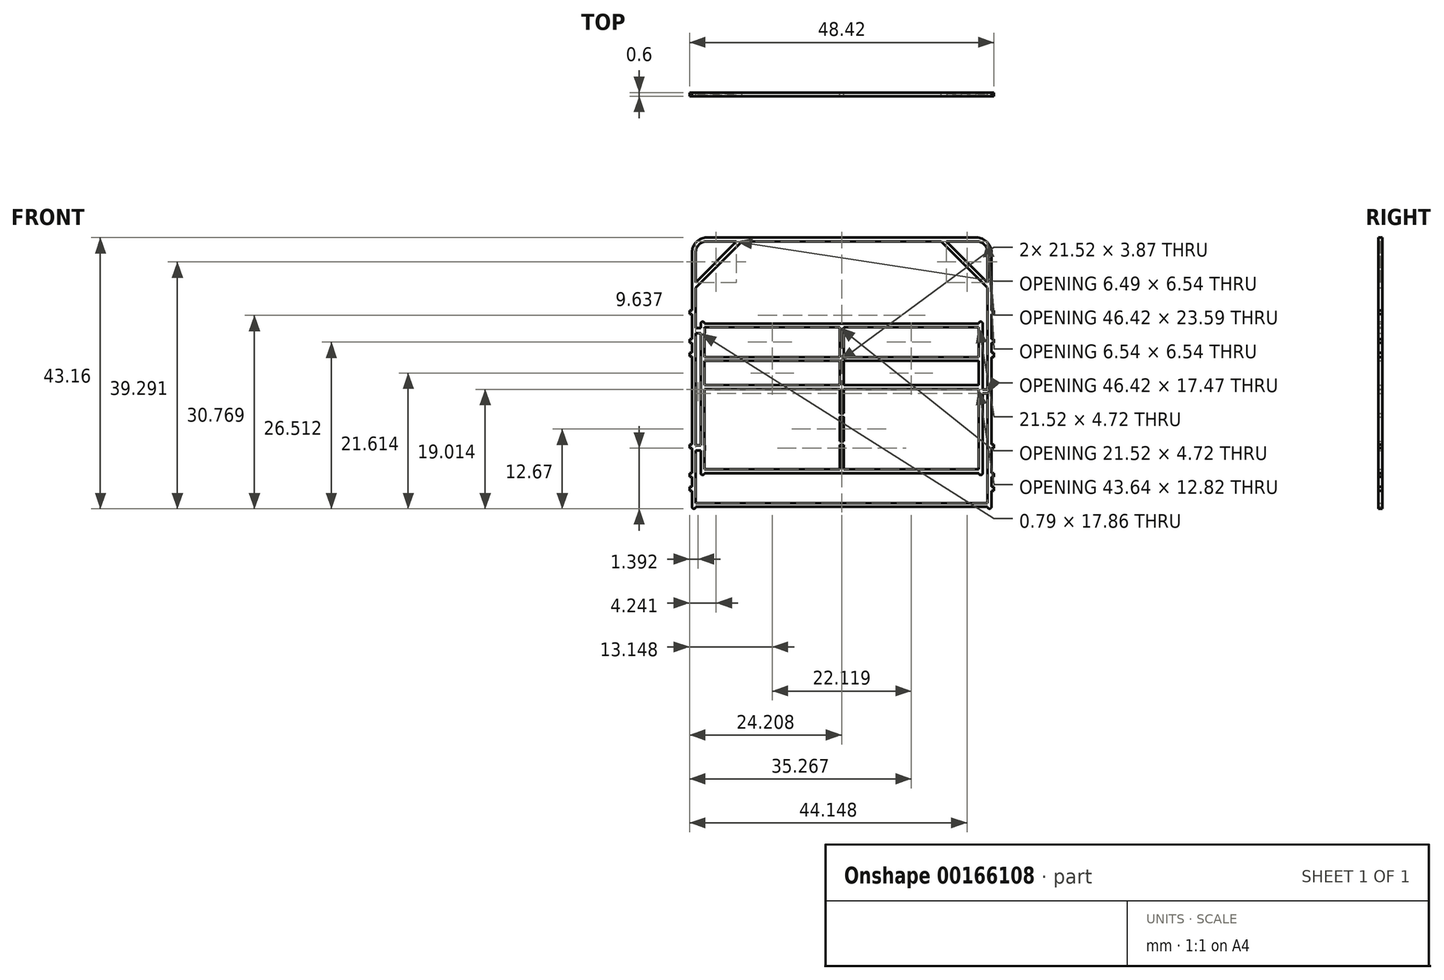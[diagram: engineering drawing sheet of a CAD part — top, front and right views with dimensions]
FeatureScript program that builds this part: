
annotation { "Feature Type Name" : "Feature", "Feature Type Description" : "" }
export const myFeature = defineFeature(function(context is Context, id is Id, definition is map)
    precondition{}
    {
        {
            var Q0;
            Q0=qCreatedBy(makeId("Front.planeOp"),FACE);
            var sketch = newSketch(context, id + "F0", { "sketchPlane" : qUnion([Q0])});
            skLineSegment(sketch, "E0.top", {"start": v(-2.38, 42.86) * mm, "end": v(-45.24, 42.86) * mm});
            skLineSegment(sketch, "E0.left", {"start": v(0, 0) * mm, "end": v(0, 40.48) * mm});
            skLineSegment(sketch, "E0.right", {"start": v(-47.63, 0) * mm, "end": v(-47.63, 40.48) * mm});
            skLineSegment(sketch, "E1.0", {"start": v(-0.6, 0.6) * mm, "end": v(-47.03, 0.6) * mm});
            skLineSegment(sketch, "E2.0", {"start": v(-47.03, 0) * mm, "end": v(-47.03, 9) * mm});
            skLineSegment(sketch, "E3.0", {"start": v(-0.6, 0) * mm, "end": v(-0.6, 40.48) * mm});
            skLineSegment(sketch, "E4.0", {"start": v(-2.38, 42.26) * mm, "end": v(-45.24, 42.26) * mm});
            skPoint(sketch, "E5.visualSharp", {"position": v(-47.63, 42.86) * mm});
            skArc(sketch, "E5.filletArc", {"start": v(-45.24, 42.86) * mm, "mid": v(-46.93, 42.17) * mm, "end": v(-47.63, 40.48) * mm});
            skArc(sketch, "E6", {"start": v(-45.24, 42.26) * mm, "mid": v(-46.5, 41.74) * mm, "end": v(-47.03, 40.48) * mm});
            skLineSegment(sketch, "E7", {"start": v(-47.03, 35.72) * mm, "end": v(-40.53, 42.26) * mm});
            skLineSegment(sketch, "E8.0", {"start": v(-46.6, 35.3) * mm, "end": v(-40.1, 41.84) * mm});
            skLineSegment(sketch, "E9", {"start": v(-46.6, 35.3) * mm, "end": v(-47.02, 34.87) * mm});
            skLineSegment(sketch, "E10", {"start": v(-40.1, 41.84) * mm, "end": v(-39.69, 42.26) * mm});
            skPoint(sketch, "E11.visualSharp", {"position": v(0, 42.86) * mm});
            skArc(sketch, "E11.filletArc", {"start": v(0, 40.48) * mm, "mid": v(-0.7, 42.17) * mm, "end": v(-2.38, 42.86) * mm});
            skPoint(sketch, "E12", {"position": v(-2.38, 42.26) * mm});
            skPoint(sketch, "E13", {"position": v(-0.6, 40.48) * mm});
            skArc(sketch, "E14", {"start": v(-0.6, 40.48) * mm, "mid": v(-1.12, 41.74) * mm, "end": v(-2.38, 42.26) * mm});
            skLineSegment(sketch, "E15", {"start": v(-7.14, 42.26) * mm, "end": v(-0.6, 35.72) * mm});
            skLineSegment(sketch, "E16.0", {"start": v(-7.57, 41.84) * mm, "end": v(-1.02, 35.3) * mm});
            skLineSegment(sketch, "E17", {"start": v(-7.57, 41.84) * mm, "end": v(-8, 42.26) * mm});
            skLineSegment(sketch, "E18", {"start": v(-1.02, 35.3) * mm, "end": v(-0.6, 34.87) * mm});
            skLineSegment(sketch, "E19", {"start": v(-45.63, 5.36) * mm, "end": v(-2, 5.36) * mm});
            skLineSegment(sketch, "E20.trimOffspring", {"start": v(-46.23, 35.67) * mm, "end": v(-46.23, 35.72) * mm, "construction": true});
            skLineSegment(sketch, "E21", {"start": v(-46.23, 5.36) * mm, "end": v(-46.23, 9) * mm});
            skLineSegment(sketch, "E22.0", {"start": v(-45.63, 5.36) * mm, "end": v(-45.63, 9) * mm});
            skLineSegment(sketch, "E23.trimOffspring", {"start": v(-1.4, 35.66) * mm, "end": v(-1.4, 35.72) * mm, "construction": true});
            skLineSegment(sketch, "E24", {"start": v(-1.4, 5.36) * mm, "end": v(-1.4, 29.18) * mm});
            skLineSegment(sketch, "E25.0", {"start": v(-2, 5.36) * mm, "end": v(-2, 29.18) * mm});
            skLineSegment(sketch, "E26", {"start": v(-45.63, 29.18) * mm, "end": v(-2, 29.18) * mm});
            skLineSegment(sketch, "E27.0", {"start": v(-45.63, 28.57) * mm, "end": v(-2, 28.58) * mm});
            skLineSegment(sketch, "E28.trimOffspring", {"start": v(-2, 5.36) * mm, "end": v(-45.63, 5.36) * mm, "construction": true});
            skLineSegment(sketch, "E29.trimOffspring", {"start": v(-2, 5.96) * mm, "end": v(-45.63, 5.96) * mm});
            skArc(sketch, "E30", {"start": v(-46.23, 5.36) * mm, "mid": v(-45.93, 5.06) * mm, "end": v(-45.63, 5.36) * mm});
            skArc(sketch, "E31", {"start": v(-2, 5.36) * mm, "mid": v(-1.7, 5.06) * mm, "end": v(-1.4, 5.36) * mm});
            skArc(sketch, "E32", {"start": v(-1.4, 29.18) * mm, "mid": v(-1.7, 29.48) * mm, "end": v(-2, 29.18) * mm});
            skArc(sketch, "E33", {"start": v(-45.63, 29.18) * mm, "mid": v(-45.93, 29.47) * mm, "end": v(-46.23, 29.18) * mm});
            skArc(sketch, "E34", {"start": v(-47.63, 0) * mm, "mid": v(-47.33, -0.3) * mm, "end": v(-47.03, 0) * mm});
            skArc(sketch, "E35", {"start": v(-0.6, 0) * mm, "mid": v(-0.3, -0.3) * mm, "end": v(0, 0) * mm});
            skLineSegment(sketch, "E36.trimOffspring", {"start": v(-0.6, 0) * mm, "end": v(-47.03, 0) * mm});
            skLineSegment(sketch, "E37.trimOffspring", {"start": v(-46.23, 35.72) * mm, "end": v(-46.18, 35.72) * mm, "construction": true});
            skPoint(sketch, "E38.start.orphan", {"position": v(-48.55, 42.86) * mm});
            skPoint(sketch, "E39.start.orphan", {"position": v(0, 43.64) * mm});
            skPoint(sketch, "E40.start.orphan", {"position": v(0.52, 42.86) * mm});
            skLineSegment(sketch, "E41.trimOffspring", {"start": v(-1.4, 35.72) * mm, "end": v(-1.45, 35.72) * mm, "construction": true});
            skLineSegment(sketch, "E42.0", {"start": v(-2, 9.83) * mm, "end": v(-45.63, 9.83) * mm});
            skLineSegment(sketch, "E43.0", {"start": v(-2, 10.43) * mm, "end": v(-45.63, 10.43) * mm});
            skLineSegment(sketch, "E44.0", {"start": v(-2, 14.3) * mm, "end": v(-45.63, 14.3) * mm});
            skLineSegment(sketch, "E45.0", {"start": v(-2, 14.9) * mm, "end": v(-45.63, 14.9) * mm});
            skLineSegment(sketch, "E46.0", {"start": v(-2, 18.78) * mm, "end": v(-45.63, 18.78) * mm});
            skLineSegment(sketch, "E47.0", {"start": v(-2, 19.38) * mm, "end": v(-45.63, 19.38) * mm});
            skLineSegment(sketch, "E48.0", {"start": v(-2, 23.25) * mm, "end": v(-45.63, 23.25) * mm});
            skLineSegment(sketch, "E49.0", {"start": v(-2, 23.85) * mm, "end": v(-45.63, 23.85) * mm});
            skPoint(sketch, "E50.endSnap0", {"position": v(-23.81, 28.58) * mm});
            skLineSegment(sketch, "E51.0", {"start": v(-24.11, 28.58) * mm, "end": v(-24.11, 23.85) * mm});
            skLineSegment(sketch, "E52.0", {"start": v(-23.51, 28.58) * mm, "end": v(-23.51, 23.85) * mm});
            skPoint(sketch, "E50.start.orphan", {"position": v(-23.81, 30.6) * mm});
            skPoint(sketch, "E53.orphan", {"position": v(-2, 30.6) * mm});
            skPoint(sketch, "E54.orphan", {"position": v(-45.63, 30.6) * mm});
            skPoint(sketch, "E55.orphan", {"position": v(-23.81, 2.6) * mm});
            skLineSegment(sketch, "E56.trimOffspring", {"start": v(-24.11, 14.3) * mm, "end": v(-24.11, 10.43) * mm});
            skLineSegment(sketch, "E57.trimOffspring", {"start": v(-23.51, 14.3) * mm, "end": v(-23.51, 10.43) * mm});
            skLineSegment(sketch, "E58.trimOffspring", {"start": v(-24.11, 9.83) * mm, "end": v(-24.11, 5.96) * mm});
            skLineSegment(sketch, "E59.trimOffspring", {"start": v(-23.51, 9.83) * mm, "end": v(-23.51, 5.96) * mm});
            skLineSegment(sketch, "E60.trimOffspring", {"start": v(-23.51, 18.78) * mm, "end": v(-23.51, 14.9) * mm});
            skLineSegment(sketch, "E61.trimOffspring", {"start": v(-24.11, 18.78) * mm, "end": v(-24.11, 14.9) * mm});
            skLineSegment(sketch, "E62.trimOffspring", {"start": v(-24.11, 23.25) * mm, "end": v(-24.11, 19.38) * mm});
            skLineSegment(sketch, "E63.trimOffspring", {"start": v(-23.51, 23.25) * mm, "end": v(-23.51, 19.38) * mm});
            skLineSegment(sketch, "E64.bottom", {"start": v(-45.58, 9.79) * mm, "end": v(-47.62, 9.79) * mm});
            skLineSegment(sketch, "E64.top", {"start": v(-45.58, 9) * mm, "end": v(-47.63, 9) * mm});
            skLineSegment(sketch, "E64.left", {"start": v(-45.58, 9.79) * mm, "end": v(-45.58, 9) * mm});
            skLineSegment(sketch, "E64.right", {"start": v(-47.63, 9.79) * mm, "end": v(-47.63, 9) * mm});
            skLineSegment(sketch, "E65.trimOffspring", {"start": v(-47.03, 9.79) * mm, "end": v(-47.03, 27.64) * mm});
            skLineSegment(sketch, "E66.trimOffspring", {"start": v(-46.23, 9.79) * mm, "end": v(-46.23, 27.64) * mm});
            skLineSegment(sketch, "E67.trimOffspring", {"start": v(-45.63, 9.79) * mm, "end": v(-45.63, 27.64) * mm});
            skLineSegment(sketch, "E68.bottom", {"start": v(-45.57, 28.44) * mm, "end": v(-47.63, 28.44) * mm});
            skLineSegment(sketch, "E68.top", {"start": v(-45.57, 27.64) * mm, "end": v(-47.63, 27.64) * mm});
            skLineSegment(sketch, "E68.left", {"start": v(-45.57, 28.44) * mm, "end": v(-45.57, 27.64) * mm});
            skLineSegment(sketch, "E68.right", {"start": v(-47.63, 28.44) * mm, "end": v(-47.63, 27.64) * mm});
            skLineSegment(sketch, "E69.trimOffspring", {"start": v(-46.23, 28.44) * mm, "end": v(-46.23, 29.18) * mm});
            skLineSegment(sketch, "E70.trimOffspring", {"start": v(-45.63, 28.44) * mm, "end": v(-45.63, 29.18) * mm});
            skLineSegment(sketch, "E71.trimOffspring", {"start": v(-47.03, 28.44) * mm, "end": v(-47.03, 40.48) * mm});
            skLineSegment(sketch, "E72.bottom", {"start": v(-47.63, 5.36) * mm, "end": v(-48.02, 5.36) * mm});
            skLineSegment(sketch, "E72.top", {"start": v(-47.62, 4.77) * mm, "end": v(-48.02, 4.77) * mm});
            skLineSegment(sketch, "E72.left", {"start": v(-47.63, 5.36) * mm, "end": v(-47.63, 4.77) * mm});
            skLineSegment(sketch, "E72.right", {"start": v(-48.02, 5.36) * mm, "end": v(-48.02, 4.77) * mm});
            skLineSegment(sketch, "E73.bottom", {"start": v(-48.02, 3.18) * mm, "end": v(-47.63, 3.18) * mm});
            skLineSegment(sketch, "E73.top", {"start": v(-48.02, 2.58) * mm, "end": v(-47.63, 2.58) * mm});
            skLineSegment(sketch, "E73.left", {"start": v(-48.02, 3.18) * mm, "end": v(-48.02, 2.58) * mm});
            skLineSegment(sketch, "E73.right", {"start": v(-47.63, 3.18) * mm, "end": v(-47.63, 2.58) * mm});
            skLineSegment(sketch, "E74.bottom", {"start": v(-48.02, 9.93) * mm, "end": v(-47.62, 9.93) * mm});
            skLineSegment(sketch, "E74.top", {"start": v(-48.02, 9.33) * mm, "end": v(-47.62, 9.33) * mm});
            skLineSegment(sketch, "E74.left", {"start": v(-48.02, 9.93) * mm, "end": v(-48.02, 9.33) * mm});
            skLineSegment(sketch, "E74.right", {"start": v(-47.63, 9.93) * mm, "end": v(-47.63, 9.33) * mm});
            skLineSegment(sketch, "E75.bottom", {"start": v(0, 3.18) * mm, "end": v(0.4, 3.18) * mm});
            skLineSegment(sketch, "E75.top", {"start": v(0, 2.58) * mm, "end": v(0.4, 2.58) * mm});
            skLineSegment(sketch, "E75.left", {"start": v(0, 3.18) * mm, "end": v(0, 2.58) * mm});
            skLineSegment(sketch, "E75.right", {"start": v(0.4, 3.18) * mm, "end": v(0.4, 2.58) * mm});
            skLineSegment(sketch, "E76.bottom", {"start": v(0, 5.36) * mm, "end": v(0.4, 5.36) * mm});
            skLineSegment(sketch, "E76.top", {"start": v(0, 4.77) * mm, "end": v(0.4, 4.77) * mm});
            skLineSegment(sketch, "E76.left", {"start": v(0, 5.36) * mm, "end": v(0, 4.77) * mm});
            skLineSegment(sketch, "E76.right", {"start": v(0.4, 5.36) * mm, "end": v(0.4, 4.77) * mm});
            skLineSegment(sketch, "E77.bottom", {"start": v(0, 9.93) * mm, "end": v(0.4, 9.93) * mm});
            skLineSegment(sketch, "E77.top", {"start": v(0, 9.33) * mm, "end": v(0.4, 9.33) * mm});
            skLineSegment(sketch, "E77.left", {"start": v(0, 9.93) * mm, "end": v(0, 9.33) * mm});
            skLineSegment(sketch, "E77.right", {"start": v(0.4, 9.93) * mm, "end": v(0.4, 9.33) * mm});
            skLineSegment(sketch, "E78.bottom", {"start": v(-47.63, 24.52) * mm, "end": v(-48.02, 24.52) * mm});
            skLineSegment(sketch, "E78.top", {"start": v(-47.63, 23.93) * mm, "end": v(-48.02, 23.93) * mm});
            skLineSegment(sketch, "E78.left", {"start": v(-47.63, 24.52) * mm, "end": v(-47.63, 23.93) * mm});
            skLineSegment(sketch, "E78.right", {"start": v(-48.02, 24.52) * mm, "end": v(-48.02, 23.93) * mm});
            skLineSegment(sketch, "E79.bottom", {"start": v(-47.63, 26.7) * mm, "end": v(-48.02, 26.7) * mm});
            skLineSegment(sketch, "E79.top", {"start": v(-47.63, 26.1) * mm, "end": v(-48.02, 26.1) * mm});
            skLineSegment(sketch, "E79.left", {"start": v(-47.63, 26.7) * mm, "end": v(-47.63, 26.1) * mm});
            skLineSegment(sketch, "E79.right", {"start": v(-48.02, 26.7) * mm, "end": v(-48.02, 26.1) * mm});
            skLineSegment(sketch, "E80.bottom", {"start": v(-47.63, 31.27) * mm, "end": v(-48.02, 31.27) * mm});
            skLineSegment(sketch, "E80.top", {"start": v(-47.63, 30.67) * mm, "end": v(-48.02, 30.67) * mm});
            skLineSegment(sketch, "E80.left", {"start": v(-47.63, 31.27) * mm, "end": v(-47.63, 30.67) * mm});
            skLineSegment(sketch, "E80.right", {"start": v(-48.02, 31.27) * mm, "end": v(-48.02, 30.67) * mm});
            skLineSegment(sketch, "E81.bottom", {"start": v(0, 24.52) * mm, "end": v(0.4, 24.52) * mm});
            skLineSegment(sketch, "E81.top", {"start": v(0, 23.85) * mm, "end": v(0.4, 23.85) * mm});
            skLineSegment(sketch, "E81.left", {"start": v(0, 24.52) * mm, "end": v(0, 23.85) * mm});
            skLineSegment(sketch, "E81.right", {"start": v(0.4, 24.52) * mm, "end": v(0.4, 23.85) * mm});
            skLineSegment(sketch, "E82.bottom", {"start": v(0, 26.7) * mm, "end": v(0.4, 26.7) * mm});
            skLineSegment(sketch, "E82.top", {"start": v(0, 26.1) * mm, "end": v(0.4, 26.1) * mm});
            skLineSegment(sketch, "E82.left", {"start": v(0, 26.7) * mm, "end": v(0, 26.1) * mm});
            skLineSegment(sketch, "E82.right", {"start": v(0.4, 26.7) * mm, "end": v(0.4, 26.1) * mm});
            skLineSegment(sketch, "E83.bottom", {"start": v(0, 31.27) * mm, "end": v(0.4, 31.27) * mm});
            skLineSegment(sketch, "E83.top", {"start": v(0, 30.67) * mm, "end": v(0.4, 30.67) * mm});
            skLineSegment(sketch, "E83.left", {"start": v(0, 31.27) * mm, "end": v(0, 30.67) * mm});
            skLineSegment(sketch, "E83.right", {"start": v(0.4, 31.27) * mm, "end": v(0.4, 30.67) * mm});
            skLineSegment(sketch, "E84.bottom", {"start": v(-2, 14.3) * mm, "end": v(-3.58, 14.3) * mm});
            skLineSegment(sketch, "E84.top", {"start": v(-2, 10.43) * mm, "end": v(-3.58, 10.43) * mm});
            skLineSegment(sketch, "E84.left", {"start": v(-2, 14.3) * mm, "end": v(-2, 10.43) * mm});
            skLineSegment(sketch, "E84.right", {"start": v(-3.58, 14.3) * mm, "end": v(-3.58, 10.43) * mm});
            skLineSegment(sketch, "E85.bottom", {"start": v(-9.52, 18.78) * mm, "end": v(-2, 18.78) * mm});
            skLineSegment(sketch, "E85.right", {"start": v(-2, 18.78) * mm, "end": v(-2, 17.98) * mm});
            skLineSegment(sketch, "E86", {"start": v(-2, 17.98) * mm, "end": v(-5.96, 17.98) * mm});
            skLineSegment(sketch, "E87", {"start": v(-5.96, 17.98) * mm, "end": v(-5.96, 18.78) * mm});
            skLineSegment(sketch, "E88", {"start": v(-3.58, 14.9) * mm, "end": v(-3.58, 17.98) * mm});
            skLineSegment(sketch, "E89.bottom", {"start": v(-1.4, 18.67) * mm, "end": v(-0.6, 18.67) * mm});
            skLineSegment(sketch, "E89.top", {"start": v(-1.4, 18.07) * mm, "end": v(-0.6, 18.07) * mm});
            skLineSegment(sketch, "E89.left", {"start": v(-1.4, 18.67) * mm, "end": v(-1.4, 18.07) * mm});
            skLineSegment(sketch, "E89.right", {"start": v(-0.6, 18.67) * mm, "end": v(-0.6, 18.07) * mm});
            skSolve(sketch);
        }
        {
            var Q0;
            {var subQ1=sQuery(id+"F0.wireOp",EDGE,"E7");Q0=makeQuery(id+"F0.imprint","IMPRINT",FACE,{"disambiguationData":[TD([[makeQuery(id+"F0.imprint","IMPRINT",EDGE,{"derivedFrom":subQ1}),-1.0]])]});}
            var Q1;
            Q1=makeQuery(id+"F0.imprint","IMPRINT",FACE,{"disambiguationData":[TD([[makeQuery(id+"F0.imprint","IMPRINT",EDGE,{"derivedFrom":sQuery(id+"F0.wireOp",EDGE,"E0.top")}),1.0]])]});
            var Q2;
            {var subQ0=sQuery(id+"F0.wireOp",EDGE,"E15");Q2=makeQuery(id+"F0.imprint","IMPRINT",FACE,{"disambiguationData":[TD([[makeQuery(id+"F0.imprint","IMPRINT",EDGE,{"derivedFrom":subQ0}),-1.0]])]});}
            var Q3;
            {var subQ4=sQuery(id+"F0.wireOp",EDGE,"E26");Q3=makeQuery(id+"F0.imprint","IMPRINT",FACE,{"disambiguationData":[TD([[makeQuery(id+"F0.imprint","IMPRINT",EDGE,{"derivedFrom":subQ4}),-1.0]])]});}
            var Q4;
            {var subQ1=sQuery(id+"F0.wireOp",EDGE,"E48.0");var subQ5=sQuery(id+"F0.wireOp",EDGE,"E25.0");var subQ6=makeQuery(id+"F0.imprint","INTERSECT",VERTEX,{"derivedFrom":[subQ5,subQ1]});Q4=makeQuery(id+"F0.imprint","IMPRINT",FACE,{"disambiguationData":[TD([[makeQuery(id+"F0.imprint","IMPRINT",EDGE,{"disambiguationData":[TD([[subQ6,-1.0]])],"derivedFrom":subQ5}),1.0]])]});}
            var Q5;
            {var subQ1=sQuery(id+"F0.wireOp",EDGE,"E46.0");var subQ4=sQuery(id+"F0.wireOp",EDGE,"E85.bottom");var subQ5=makeQuery(id+"F0.imprint","INTERSECT",VERTEX,{"derivedFrom":[subQ1,subQ4]});Q5=makeQuery(id+"F0.imprint","IMPRINT",FACE,{"disambiguationData":[TD([[makeQuery(id+"F0.imprint","IMPRINT",EDGE,{"disambiguationData":[TD([[subQ5,-1.0]])],"derivedFrom":subQ1}),-1.0]])]});}
            var Q6;
            {var subQ5=sQuery(id+"F0.wireOp",EDGE,"E84.bottom");Q6=makeQuery(id+"F0.imprint","IMPRINT",FACE,{"disambiguationData":[TD([[makeQuery(id+"F0.imprint","IMPRINT",EDGE,{"derivedFrom":subQ5}),-1.0]])]});}
            var Q7;
            {var subQ7=sQuery(id+"F0.wireOp",EDGE,"E84.top");Q7=makeQuery(id+"F0.imprint","IMPRINT",FACE,{"disambiguationData":[TD([[makeQuery(id+"F0.imprint","IMPRINT",EDGE,{"derivedFrom":subQ7}),1.0]])]});}
            var Q8;
            {var subQ5=sQuery(id+"F0.wireOp",EDGE,"E19");Q8=makeQuery(id+"F0.imprint","IMPRINT",FACE,{"disambiguationData":[TD([[makeQuery(id+"F0.imprint","IMPRINT",EDGE,{"derivedFrom":subQ5}),1.0]])]});}
            var Q9;
            {var subQ0=sQuery(id+"F0.wireOp",EDGE,"E58.trimOffspring");Q9=makeQuery(id+"F0.imprint","IMPRINT",FACE,{"disambiguationData":[TD([[makeQuery(id+"F0.imprint","IMPRINT",EDGE,{"derivedFrom":subQ0}),1.0]])]});}
            var Q10;
            {var subQ0=sQuery(id+"F0.wireOp",EDGE,"E56.trimOffspring");Q10=makeQuery(id+"F0.imprint","IMPRINT",FACE,{"disambiguationData":[TD([[makeQuery(id+"F0.imprint","IMPRINT",EDGE,{"derivedFrom":subQ0}),1.0]])]});}
            var Q11;
            {var subQ0=sQuery(id+"F0.wireOp",EDGE,"E60.trimOffspring");Q11=makeQuery(id+"F0.imprint","IMPRINT",FACE,{"disambiguationData":[TD([[makeQuery(id+"F0.imprint","IMPRINT",EDGE,{"derivedFrom":subQ0}),-1.0]])]});}
            var Q12;
            {var subQ0=sQuery(id+"F0.wireOp",EDGE,"E62.trimOffspring");Q12=makeQuery(id+"F0.imprint","IMPRINT",FACE,{"disambiguationData":[TD([[makeQuery(id+"F0.imprint","IMPRINT",EDGE,{"derivedFrom":subQ0}),1.0]])]});}
            var Q13;
            {var subQ0=sQuery(id+"F0.wireOp",EDGE,"E51.0");Q13=makeQuery(id+"F0.imprint","IMPRINT",FACE,{"disambiguationData":[TD([[makeQuery(id+"F0.imprint","IMPRINT",EDGE,{"derivedFrom":subQ0}),1.0]])]});}
            var Q14;
            {var subQ9=sQuery(id+"F0.wireOp",EDGE,"E66.trimOffspring");Q14=makeQuery(id+"F0.imprint","IMPRINT",FACE,{"disambiguationData":[TD([[makeQuery(id+"F0.imprint","IMPRINT",EDGE,{"derivedFrom":subQ9}),-1.0]])]});}
            var Q15;
            {var subQ5=sQuery(id+"F0.wireOp",EDGE,"E33");Q15=makeQuery(id+"F0.imprint","IMPRINT",FACE,{"disambiguationData":[TD([[makeQuery(id+"F0.imprint","IMPRINT",EDGE,{"derivedFrom":subQ5}),1.0]])]});}
            var Q16;
            {var subQ5=sQuery(id+"F0.wireOp",EDGE,"E21");Q16=makeQuery(id+"F0.imprint","IMPRINT",FACE,{"disambiguationData":[TD([[makeQuery(id+"F0.imprint","IMPRINT",EDGE,{"derivedFrom":subQ5}),-1.0]])]});}
            var Q17;
            {var subQ5=sQuery(id+"F0.wireOp",EDGE,"E31");Q17=makeQuery(id+"F0.imprint","IMPRINT",FACE,{"disambiguationData":[TD([[makeQuery(id+"F0.imprint","IMPRINT",EDGE,{"derivedFrom":subQ5}),1.0]])]});}
            var Q18;
            {var subQ3=sQuery(id+"F0.wireOp",EDGE,"E65.trimOffspring");Q18=makeQuery(id+"F0.imprint","IMPRINT",FACE,{"disambiguationData":[TD([[makeQuery(id+"F0.imprint","IMPRINT",EDGE,{"derivedFrom":subQ3}),1.0]])]});}
            var Q19;
            {var subQ2=sQuery(id+"F0.wireOp",EDGE,"E34");Q19=makeQuery(id+"F0.imprint","IMPRINT",FACE,{"disambiguationData":[TD([[makeQuery(id+"F0.imprint","IMPRINT",EDGE,{"derivedFrom":subQ2}),1.0]])]});}
            var Q20;
            Q20=makeQuery(id+"F0.imprint","IMPRINT",FACE,{"disambiguationData":[TD([[makeQuery(id+"F0.imprint","IMPRINT",EDGE,{"derivedFrom":sQuery(id+"F0.wireOp",EDGE,"E89.bottom")}),-1.0]])]});
            var Q21;
            {var subQ0=sQuery(id+"F0.wireOp",EDGE,"E1.0");Q21=makeQuery(id+"F0.imprint","IMPRINT",FACE,{"disambiguationData":[TD([[makeQuery(id+"F0.imprint","IMPRINT",EDGE,{"derivedFrom":subQ0}),1.0]])]});}
            var Q22;
            Q22=makeQuery(id+"F0.imprint","IMPRINT",FACE,{"disambiguationData":[TD([[makeQuery(id+"F0.imprint","IMPRINT",EDGE,{"derivedFrom":sQuery(id+"F0.wireOp",EDGE,"E80.bottom")}),1.0]])]});
            var Q23;
            Q23=makeQuery(id+"F0.imprint","IMPRINT",FACE,{"disambiguationData":[TD([[makeQuery(id+"F0.imprint","IMPRINT",EDGE,{"derivedFrom":sQuery(id+"F0.wireOp",EDGE,"E79.bottom")}),1.0]])]});
            var Q24;
            Q24=makeQuery(id+"F0.imprint","IMPRINT",FACE,{"disambiguationData":[TD([[makeQuery(id+"F0.imprint","IMPRINT",EDGE,{"derivedFrom":sQuery(id+"F0.wireOp",EDGE,"E78.bottom")}),1.0]])]});
            var Q25;
            {var subQ2=sQuery(id+"F0.wireOp",EDGE,"E74.bottom");Q25=makeQuery(id+"F0.imprint","IMPRINT",FACE,{"disambiguationData":[TD([[makeQuery(id+"F0.imprint","IMPRINT",EDGE,{"derivedFrom":subQ2}),-1.0]])]});}
            var Q26;
            Q26=makeQuery(id+"F0.imprint","IMPRINT",FACE,{"disambiguationData":[TD([[makeQuery(id+"F0.imprint","IMPRINT",EDGE,{"derivedFrom":sQuery(id+"F0.wireOp",EDGE,"E72.bottom")}),1.0]])]});
            var Q27;
            Q27=makeQuery(id+"F0.imprint","IMPRINT",FACE,{"disambiguationData":[TD([[makeQuery(id+"F0.imprint","IMPRINT",EDGE,{"derivedFrom":sQuery(id+"F0.wireOp",EDGE,"E73.bottom")}),-1.0]])]});
            var Q28;
            Q28=makeQuery(id+"F0.imprint","IMPRINT",FACE,{"disambiguationData":[TD([[makeQuery(id+"F0.imprint","IMPRINT",EDGE,{"derivedFrom":sQuery(id+"F0.wireOp",EDGE,"E75.bottom")}),-1.0]])]});
            var Q29;
            Q29=makeQuery(id+"F0.imprint","IMPRINT",FACE,{"disambiguationData":[TD([[makeQuery(id+"F0.imprint","IMPRINT",EDGE,{"derivedFrom":sQuery(id+"F0.wireOp",EDGE,"E76.bottom")}),-1.0]])]});
            var Q30;
            Q30=makeQuery(id+"F0.imprint","IMPRINT",FACE,{"disambiguationData":[TD([[makeQuery(id+"F0.imprint","IMPRINT",EDGE,{"derivedFrom":sQuery(id+"F0.wireOp",EDGE,"E77.bottom")}),-1.0]])]});
            var Q31;
            Q31=makeQuery(id+"F0.imprint","IMPRINT",FACE,{"disambiguationData":[TD([[makeQuery(id+"F0.imprint","IMPRINT",EDGE,{"derivedFrom":sQuery(id+"F0.wireOp",EDGE,"E83.bottom")}),-1.0]])]});
            var Q32;
            Q32=makeQuery(id+"F0.imprint","IMPRINT",FACE,{"disambiguationData":[TD([[makeQuery(id+"F0.imprint","IMPRINT",EDGE,{"derivedFrom":sQuery(id+"F0.wireOp",EDGE,"E82.bottom")}),-1.0]])]});
            var Q33;
            Q33=makeQuery(id+"F0.imprint","IMPRINT",FACE,{"disambiguationData":[TD([[makeQuery(id+"F0.imprint","IMPRINT",EDGE,{"derivedFrom":sQuery(id+"F0.wireOp",EDGE,"E81.bottom")}),-1.0]])]});
            var Q34;
            {var subQ6=sQuery(id+"F0.wireOp",EDGE,"E68.left");Q34=makeQuery(id+"F0.imprint","IMPRINT",FACE,{"disambiguationData":[TD([[makeQuery(id+"F0.imprint","IMPRINT",EDGE,{"derivedFrom":subQ6}),-1.0]])]});}
            var Q35;
            {var subQ3=sQuery(id+"F0.wireOp",EDGE,"E64.left");Q35=makeQuery(id+"F0.imprint","IMPRINT",FACE,{"disambiguationData":[TD([[makeQuery(id+"F0.imprint","IMPRINT",EDGE,{"derivedFrom":subQ3}),-1.0]])]});}
            extrude(context, id + "F1", {"entities" : qUnion([Q0, Q1, Q2, Q3, Q4, Q5, Q6, Q7, Q8, Q9, Q10, Q11, Q12, Q13, Q14, Q15, Q16, Q17, Q18, Q19, Q20, Q21, Q22, Q23, Q24, Q25, Q26, Q27, Q28, Q29, Q30, Q31, Q32, Q33, Q34, Q35]), "depth" : .6 * mm, "symmetric" : true});
        }
        {
            var Q0;
            Q0=makeQuery(id+"F1.opExtrude","CAP_EDGE",EDGE,{"disambiguationData":[OSD([sQuery(id+"F0.wireOp",EDGE,"E0.top")])],"isStart":false});
            var Q1;
            {var subQ0=sQuery(id+"F0.wireOp",EDGE,"E4.0");Q1=makeQuery(id+"F1.opExtrude","CAP_EDGE",EDGE,{"disambiguationData":[OSD([subQ0]),TDD([makeQuery(id+"F0.imprint","IMPRINT",EDGE,{"disambiguationData":[TD([[makeQuery(id+"F0.imprint","INTERSECT",VERTEX,{"derivedFrom":[subQ0,sQuery(id+"F0.wireOp",EDGE,"E10")]}),1.0]])],"derivedFrom":subQ0})])],"isStart":false});}
            var Q2;
            Q2=makeQuery(id+"F1.opExtrude","SWEPT_FACE",FACE,{"disambiguationData":[OSD([sQuery(id+"F0.wireOp",EDGE,"E0.top")])]});
            var Q3;
            Q3=makeQuery(id+"F1.opExtrude","CAP_EDGE",EDGE,{"disambiguationData":[OSD([sQuery(id+"F0.wireOp",EDGE,"E11.filletArc")])],"isStart":false});
            var Q4;
            Q4=makeQuery(id+"F1.opExtrude","CAP_EDGE",EDGE,{"disambiguationData":[OSD([sQuery(id+"F0.wireOp",EDGE,"E11.filletArc")])],"isStart":true});
            var Q5;
            Q5=makeQuery(id+"F1.opExtrude","CAP_EDGE",EDGE,{"disambiguationData":[OSD([sQuery(id+"F0.wireOp",EDGE,"E14")])],"isStart":false});
            var Q6;
            {var subQ0=sQuery(id+"F0.wireOp",EDGE,"E4.0");Q6=makeQuery(id+"F1.opExtrude","CAP_EDGE",EDGE,{"disambiguationData":[OSD([subQ0]),TDD([makeQuery(id+"F0.imprint","IMPRINT",EDGE,{"disambiguationData":[TD([[makeQuery(id+"F0.imprint","INTERSECT",VERTEX,{"derivedFrom":[subQ0,sQuery(id+"F0.wireOp",EDGE,"E14")]}),-1.0]])],"derivedFrom":subQ0})])],"isStart":false});}
            var Q7;
            Q7=makeQuery(id+"F1.opExtrude","CAP_EDGE",EDGE,{"disambiguationData":[OSD([sQuery(id+"F0.wireOp",EDGE,"E15")])],"isStart":false});
            var Q8;
            Q8=makeQuery(id+"F1.opExtrude","CAP_EDGE",EDGE,{"disambiguationData":[OSD([sQuery(id+"F0.wireOp",EDGE,"E15")])],"isStart":true});
            var Q9;
            Q9=makeQuery(id+"F1.opExtrude","CAP_EDGE",EDGE,{"disambiguationData":[OSD([sQuery(id+"F0.wireOp",EDGE,"E16.0"),sQuery(id+"F0.wireOp",EDGE,"E17"),sQuery(id+"F0.wireOp",EDGE,"E18")])],"isStart":false});
            var Q10;
            {var subQ0=sQuery(id+"F0.wireOp",EDGE,"E3.0");Q10=makeQuery(id+"F1.opExtrude","CAP_EDGE",EDGE,{"disambiguationData":[OSD([subQ0]),TDD([makeQuery(id+"F0.imprint","IMPRINT",EDGE,{"disambiguationData":[TD([[makeQuery(id+"F0.imprint","INTERSECT",VERTEX,{"derivedFrom":[subQ0,sQuery(id+"F0.wireOp",EDGE,"E14")]}),1.0]])],"derivedFrom":subQ0})])],"isStart":false});}
            var Q11;
            {var subQ0=sQuery(id+"F0.wireOp",EDGE,"E0.left");Q11=makeQuery(id+"F1.opExtrude","CAP_EDGE",EDGE,{"disambiguationData":[OSD([subQ0]),TDD([makeQuery(id+"F0.imprint","IMPRINT",EDGE,{"disambiguationData":[TD([[makeQuery(id+"F0.imprint","INTERSECT",VERTEX,{"derivedFrom":[subQ0,sQuery(id+"F0.wireOp",EDGE,"E11.filletArc")]}),1.0]])],"derivedFrom":subQ0})])],"isStart":false});}
            var Q12;
            {var subQ0=sQuery(id+"F0.wireOp",EDGE,"E0.left");Q12=makeQuery(id+"F1.opExtrude","CAP_EDGE",EDGE,{"disambiguationData":[OSD([subQ0]),TDD([makeQuery(id+"F0.imprint","IMPRINT",EDGE,{"disambiguationData":[TD([[makeQuery(id+"F0.imprint","INTERSECT",VERTEX,{"derivedFrom":[subQ0,sQuery(id+"F0.wireOp",EDGE,"E11.filletArc")]}),1.0]])],"derivedFrom":subQ0})])],"isStart":true});}
            var Q13;
            {var subQ0=sQuery(id+"F0.wireOp",EDGE,"E3.0");Q13=makeQuery(id+"F1.opExtrude","CAP_EDGE",EDGE,{"disambiguationData":[OSD([subQ0]),TDD([makeQuery(id+"F0.imprint","IMPRINT",EDGE,{"disambiguationData":[TD([[makeQuery(id+"F0.imprint","INTERSECT",VERTEX,{"derivedFrom":[subQ0,sQuery(id+"F0.wireOp",EDGE,"E18")]}),1.0]])],"derivedFrom":subQ0})])],"isStart":false});}
            var Q14;
            Q14=makeQuery(id+"F1.opExtrude","CAP_EDGE",EDGE,{"disambiguationData":[OSD([sQuery(id+"F0.wireOp",EDGE,"E83.right")])],"isStart":false});
            var Q15;
            Q15=makeQuery(id+"F1.opExtrude","CAP_EDGE",EDGE,{"disambiguationData":[OSD([sQuery(id+"F0.wireOp",EDGE,"E83.right")])],"isStart":true});
            var Q16;
            {var subQ0=sQuery(id+"F0.wireOp",EDGE,"E0.left");Q16=makeQuery(id+"F1.opExtrude","CAP_EDGE",EDGE,{"disambiguationData":[OSD([subQ0]),TDD([makeQuery(id+"F0.imprint","IMPRINT",EDGE,{"disambiguationData":[TD([[makeQuery(id+"F0.imprint","INTERSECT",VERTEX,{"derivedFrom":[subQ0,sQuery(id+"F0.wireOp",EDGE,"E82.bottom"),sQuery(id+"F0.wireOp",EDGE,"E82.left")]}),-1.0]])],"derivedFrom":subQ0})])],"isStart":false});}
            var Q17;
            {var subQ0=sQuery(id+"F0.wireOp",EDGE,"E0.left");Q17=makeQuery(id+"F1.opExtrude","CAP_EDGE",EDGE,{"disambiguationData":[OSD([subQ0]),TDD([makeQuery(id+"F0.imprint","IMPRINT",EDGE,{"disambiguationData":[TD([[makeQuery(id+"F0.imprint","INTERSECT",VERTEX,{"derivedFrom":[subQ0,sQuery(id+"F0.wireOp",EDGE,"E82.bottom"),sQuery(id+"F0.wireOp",EDGE,"E82.left")]}),-1.0]])],"derivedFrom":subQ0})])],"isStart":true});}
            var Q18;
            Q18=makeQuery(id+"F1.opExtrude","CAP_EDGE",EDGE,{"disambiguationData":[OSD([sQuery(id+"F0.wireOp",EDGE,"E82.right")])],"isStart":false});
            var Q19;
            Q19=makeQuery(id+"F1.opExtrude","CAP_EDGE",EDGE,{"disambiguationData":[OSD([sQuery(id+"F0.wireOp",EDGE,"E82.right")])],"isStart":true});
            var Q20;
            {var subQ0=sQuery(id+"F0.wireOp",EDGE,"E0.left");Q20=makeQuery(id+"F1.opExtrude","CAP_EDGE",EDGE,{"disambiguationData":[OSD([subQ0]),TDD([makeQuery(id+"F0.imprint","IMPRINT",EDGE,{"disambiguationData":[TD([[makeQuery(id+"F0.imprint","INTERSECT",VERTEX,{"derivedFrom":[subQ0,sQuery(id+"F0.wireOp",EDGE,"E81.bottom"),sQuery(id+"F0.wireOp",EDGE,"E81.left")]}),-1.0]])],"derivedFrom":subQ0})])],"isStart":false});}
            var Q21;
            {var subQ0=sQuery(id+"F0.wireOp",EDGE,"E0.left");Q21=makeQuery(id+"F1.opExtrude","CAP_EDGE",EDGE,{"disambiguationData":[OSD([subQ0]),TDD([makeQuery(id+"F0.imprint","IMPRINT",EDGE,{"disambiguationData":[TD([[makeQuery(id+"F0.imprint","INTERSECT",VERTEX,{"derivedFrom":[subQ0,sQuery(id+"F0.wireOp",EDGE,"E81.bottom"),sQuery(id+"F0.wireOp",EDGE,"E81.left")]}),-1.0]])],"derivedFrom":subQ0})])],"isStart":true});}
            var Q22;
            Q22=makeQuery(id+"F1.opExtrude","CAP_EDGE",EDGE,{"disambiguationData":[OSD([sQuery(id+"F0.wireOp",EDGE,"E81.right")])],"isStart":false});
            var Q23;
            Q23=makeQuery(id+"F1.opExtrude","CAP_EDGE",EDGE,{"disambiguationData":[OSD([sQuery(id+"F0.wireOp",EDGE,"E81.right")])],"isStart":true});
            var Q24;
            {var subQ0=sQuery(id+"F0.wireOp",EDGE,"E0.left");Q24=makeQuery(id+"F1.opExtrude","CAP_EDGE",EDGE,{"disambiguationData":[OSD([subQ0]),TDD([makeQuery(id+"F0.imprint","IMPRINT",EDGE,{"disambiguationData":[TD([[makeQuery(id+"F0.imprint","INTERSECT",VERTEX,{"derivedFrom":[subQ0,sQuery(id+"F0.wireOp",EDGE,"E77.bottom"),sQuery(id+"F0.wireOp",EDGE,"E77.left")]}),-1.0]])],"derivedFrom":subQ0})])],"isStart":false});}
            var Q25;
            {var subQ0=sQuery(id+"F0.wireOp",EDGE,"E0.left");Q25=makeQuery(id+"F1.opExtrude","CAP_EDGE",EDGE,{"disambiguationData":[OSD([subQ0]),TDD([makeQuery(id+"F0.imprint","IMPRINT",EDGE,{"disambiguationData":[TD([[makeQuery(id+"F0.imprint","INTERSECT",VERTEX,{"derivedFrom":[subQ0,sQuery(id+"F0.wireOp",EDGE,"E77.bottom"),sQuery(id+"F0.wireOp",EDGE,"E77.left")]}),-1.0]])],"derivedFrom":subQ0})])],"isStart":true});}
            var Q26;
            Q26=makeQuery(id+"F1.opExtrude","CAP_EDGE",EDGE,{"disambiguationData":[OSD([sQuery(id+"F0.wireOp",EDGE,"E89.bottom")])],"isStart":false});
            var Q27;
            Q27=makeQuery(id+"F1.opExtrude","CAP_EDGE",EDGE,{"disambiguationData":[OSD([sQuery(id+"F0.wireOp",EDGE,"E89.top")])],"isStart":false});
            var Q28;
            Q28=makeQuery(id+"F1.opExtrude","CAP_EDGE",EDGE,{"disambiguationData":[OSD([sQuery(id+"F0.wireOp",EDGE,"E89.bottom")])],"isStart":true});
            var Q29;
            {var subQ0=sQuery(id+"F0.wireOp",EDGE,"E3.0");Q29=makeQuery(id+"F1.opExtrude","CAP_EDGE",EDGE,{"disambiguationData":[OSD([subQ0]),TDD([makeQuery(id+"F0.imprint","IMPRINT",EDGE,{"disambiguationData":[TD([[makeQuery(id+"F0.imprint","INTERSECT",VERTEX,{"derivedFrom":[sQuery(id+"F0.wireOp",EDGE,"E1.0"),subQ0]}),-1.0]])],"derivedFrom":subQ0})])],"isStart":false});}
            var Q30;
            Q30=makeQuery(id+"F1.opExtrude","CAP_EDGE",EDGE,{"disambiguationData":[OSD([sQuery(id+"F0.wireOp",EDGE,"E77.right")])],"isStart":false});
            var Q31;
            Q31=makeQuery(id+"F1.opExtrude","CAP_EDGE",EDGE,{"disambiguationData":[OSD([sQuery(id+"F0.wireOp",EDGE,"E77.right")])],"isStart":true});
            var Q32;
            {var subQ0=sQuery(id+"F0.wireOp",EDGE,"E0.left");Q32=makeQuery(id+"F1.opExtrude","CAP_EDGE",EDGE,{"disambiguationData":[OSD([subQ0]),TDD([makeQuery(id+"F0.imprint","IMPRINT",EDGE,{"disambiguationData":[TD([[makeQuery(id+"F0.imprint","INTERSECT",VERTEX,{"derivedFrom":[subQ0,sQuery(id+"F0.wireOp",EDGE,"E76.bottom"),sQuery(id+"F0.wireOp",EDGE,"E76.left")]}),-1.0]])],"derivedFrom":subQ0})])],"isStart":false});}
            var Q33;
            {var subQ0=sQuery(id+"F0.wireOp",EDGE,"E0.left");Q33=makeQuery(id+"F1.opExtrude","CAP_EDGE",EDGE,{"disambiguationData":[OSD([subQ0]),TDD([makeQuery(id+"F0.imprint","IMPRINT",EDGE,{"disambiguationData":[TD([[makeQuery(id+"F0.imprint","INTERSECT",VERTEX,{"derivedFrom":[subQ0,sQuery(id+"F0.wireOp",EDGE,"E76.bottom"),sQuery(id+"F0.wireOp",EDGE,"E76.left")]}),-1.0]])],"derivedFrom":subQ0})])],"isStart":true});}
            var Q34;
            Q34=makeQuery(id+"F1.opExtrude","CAP_EDGE",EDGE,{"disambiguationData":[OSD([sQuery(id+"F0.wireOp",EDGE,"E76.right")])],"isStart":false});
            var Q35;
            Q35=makeQuery(id+"F1.opExtrude","CAP_EDGE",EDGE,{"disambiguationData":[OSD([sQuery(id+"F0.wireOp",EDGE,"E76.right")])],"isStart":true});
            var Q36;
            {var subQ0=sQuery(id+"F0.wireOp",EDGE,"E0.left");Q36=makeQuery(id+"F1.opExtrude","CAP_EDGE",EDGE,{"disambiguationData":[OSD([subQ0]),TDD([makeQuery(id+"F0.imprint","IMPRINT",EDGE,{"disambiguationData":[TD([[makeQuery(id+"F0.imprint","INTERSECT",VERTEX,{"derivedFrom":[subQ0,sQuery(id+"F0.wireOp",EDGE,"E75.bottom"),sQuery(id+"F0.wireOp",EDGE,"E75.left")]}),-1.0]])],"derivedFrom":subQ0})])],"isStart":false});}
            var Q37;
            {var subQ0=sQuery(id+"F0.wireOp",EDGE,"E0.left");Q37=makeQuery(id+"F1.opExtrude","CAP_EDGE",EDGE,{"disambiguationData":[OSD([subQ0]),TDD([makeQuery(id+"F0.imprint","IMPRINT",EDGE,{"disambiguationData":[TD([[makeQuery(id+"F0.imprint","INTERSECT",VERTEX,{"derivedFrom":[subQ0,sQuery(id+"F0.wireOp",EDGE,"E75.bottom"),sQuery(id+"F0.wireOp",EDGE,"E75.left")]}),-1.0]])],"derivedFrom":subQ0})])],"isStart":true});}
            var Q38;
            Q38=makeQuery(id+"F1.opExtrude","CAP_EDGE",EDGE,{"disambiguationData":[OSD([sQuery(id+"F0.wireOp",EDGE,"E75.right")])],"isStart":false});
            var Q39;
            Q39=makeQuery(id+"F1.opExtrude","CAP_EDGE",EDGE,{"disambiguationData":[OSD([sQuery(id+"F0.wireOp",EDGE,"E75.right")])],"isStart":true});
            var Q40;
            {var subQ0=sQuery(id+"F0.wireOp",EDGE,"E0.left");Q40=makeQuery(id+"F1.opExtrude","CAP_EDGE",EDGE,{"disambiguationData":[OSD([subQ0]),TDD([makeQuery(id+"F0.imprint","IMPRINT",EDGE,{"disambiguationData":[TD([[makeQuery(id+"F0.imprint","INTERSECT",VERTEX,{"derivedFrom":[subQ0,sQuery(id+"F0.wireOp",EDGE,"E35")]}),-1.0]])],"derivedFrom":subQ0})])],"isStart":false});}
            var Q41;
            {var subQ0=sQuery(id+"F0.wireOp",EDGE,"E0.left");Q41=makeQuery(id+"F1.opExtrude","CAP_EDGE",EDGE,{"disambiguationData":[OSD([subQ0]),TDD([makeQuery(id+"F0.imprint","IMPRINT",EDGE,{"disambiguationData":[TD([[makeQuery(id+"F0.imprint","INTERSECT",VERTEX,{"derivedFrom":[subQ0,sQuery(id+"F0.wireOp",EDGE,"E35")]}),-1.0]])],"derivedFrom":subQ0})])],"isStart":true});}
            var Q42;
            Q42=makeQuery(id+"F1.opExtrude","CAP_EDGE",EDGE,{"disambiguationData":[OSD([sQuery(id+"F0.wireOp",EDGE,"E1.0")])],"isStart":false});
            var Q43;
            Q43=makeQuery(id+"F1.opExtrude","CAP_EDGE",EDGE,{"disambiguationData":[OSD([sQuery(id+"F0.wireOp",EDGE,"E1.0")])],"isStart":true});
            var Q44;
            Q44=makeQuery(id+"F1.opExtrude","CAP_EDGE",EDGE,{"disambiguationData":[OSD([sQuery(id+"F0.wireOp",EDGE,"E36.trimOffspring")])],"isStart":false});
            var Q45;
            Q45=makeQuery(id+"F1.opExtrude","CAP_EDGE",EDGE,{"disambiguationData":[OSD([sQuery(id+"F0.wireOp",EDGE,"E35")])],"isStart":false});
            var Q46;
            Q46=makeQuery(id+"F1.opExtrude","CAP_EDGE",EDGE,{"disambiguationData":[OSD([sQuery(id+"F0.wireOp",EDGE,"E2.0")])],"isStart":false});
            var Q47;
            Q47=makeQuery(id+"F1.opExtrude","CAP_EDGE",EDGE,{"disambiguationData":[OSD([sQuery(id+"F0.wireOp",EDGE,"E2.0")])],"isStart":true});
            var Q48;
            Q48=makeQuery(id+"F1.opExtrude","CAP_EDGE",EDGE,{"disambiguationData":[OSD([sQuery(id+"F0.wireOp",EDGE,"E73.left")])],"isStart":false});
            var Q49;
            {var subQ0=sQuery(id+"F0.wireOp",EDGE,"E0.right");Q49=makeQuery(id+"F1.opExtrude","CAP_EDGE",EDGE,{"disambiguationData":[OSD([subQ0]),TDD([makeQuery(id+"F0.imprint","IMPRINT",EDGE,{"disambiguationData":[TD([[makeQuery(id+"F0.imprint","INTERSECT",VERTEX,{"derivedFrom":[subQ0,sQuery(id+"F0.wireOp",EDGE,"E72.top"),sQuery(id+"F0.wireOp",EDGE,"E72.left")]}),1.0]])],"derivedFrom":subQ0})])],"isStart":false});}
            var Q50;
            Q50=makeQuery(id+"F1.opExtrude","CAP_EDGE",EDGE,{"disambiguationData":[OSD([sQuery(id+"F0.wireOp",EDGE,"E72.right")])],"isStart":false});
            var Q51;
            Q51=makeQuery(id+"F1.opExtrude","CAP_EDGE",EDGE,{"disambiguationData":[OSD([sQuery(id+"F0.wireOp",EDGE,"E0.right"),sQuery(id+"F0.wireOp",EDGE,"E64.right")])],"isStart":false});
            var Q52;
            Q52=makeQuery(id+"F1.opExtrude","CAP_EDGE",EDGE,{"disambiguationData":[OSD([sQuery(id+"F0.wireOp",EDGE,"E74.left")])],"isStart":false});
            var Q53;
            Q53=makeQuery(id+"F1.opExtrude","CAP_EDGE",EDGE,{"disambiguationData":[OSD([sQuery(id+"F0.wireOp",EDGE,"E65.trimOffspring")])],"isStart":false});
            var Q54;
            {var subQ0=sQuery(id+"F0.wireOp",EDGE,"E0.right");Q54=makeQuery(id+"F1.opExtrude","CAP_EDGE",EDGE,{"disambiguationData":[OSD([subQ0]),TDD([makeQuery(id+"F0.imprint","IMPRINT",EDGE,{"disambiguationData":[TD([[makeQuery(id+"F0.imprint","INTERSECT",VERTEX,{"derivedFrom":[subQ0,sQuery(id+"F0.wireOp",EDGE,"E74.bottom"),sQuery(id+"F0.wireOp",EDGE,"E74.right")]}),-1.0]])],"derivedFrom":subQ0})])],"isStart":false});}
            var Q55;
            Q55=makeQuery(id+"F1.opExtrude","CAP_EDGE",EDGE,{"disambiguationData":[OSD([sQuery(id+"F0.wireOp",EDGE,"E65.trimOffspring")])],"isStart":true});
            var Q56;
            Q56=makeQuery(id+"F1.opExtrude","CAP_EDGE",EDGE,{"disambiguationData":[OSD([sQuery(id+"F0.wireOp",EDGE,"E78.right")])],"isStart":false});
            var Q57;
            Q57=makeQuery(id+"F1.opExtrude","CAP_EDGE",EDGE,{"disambiguationData":[OSD([sQuery(id+"F0.wireOp",EDGE,"E79.right")])],"isStart":false});
            var Q58;
            Q58=makeQuery(id+"F1.opExtrude","CAP_EDGE",EDGE,{"disambiguationData":[OSD([sQuery(id+"F0.wireOp",EDGE,"E0.right"),sQuery(id+"F0.wireOp",EDGE,"E68.right")])],"isStart":false});
            var Q59;
            Q59=makeQuery(id+"F1.opExtrude","CAP_EDGE",EDGE,{"disambiguationData":[OSD([sQuery(id+"F0.wireOp",EDGE,"E80.right")])],"isStart":false});
            var Q60;
            {var subQ0=sQuery(id+"F0.wireOp",EDGE,"E71.trimOffspring");Q60=makeQuery(id+"F1.opExtrude","CAP_EDGE",EDGE,{"disambiguationData":[OSD([subQ0]),TDD([makeQuery(id+"F0.imprint","IMPRINT",EDGE,{"disambiguationData":[TD([[makeQuery(id+"F0.imprint","INTERSECT",VERTEX,{"derivedFrom":[sQuery(id+"F0.wireOp",EDGE,"E9"),subQ0]}),1.0]])],"derivedFrom":subQ0})])],"isStart":false});}
            var Q61;
            {var subQ0=sQuery(id+"F0.wireOp",EDGE,"E71.trimOffspring");Q61=makeQuery(id+"F1.opExtrude","CAP_EDGE",EDGE,{"disambiguationData":[OSD([subQ0]),TDD([makeQuery(id+"F0.imprint","IMPRINT",EDGE,{"disambiguationData":[TD([[makeQuery(id+"F0.imprint","INTERSECT",VERTEX,{"derivedFrom":[sQuery(id+"F0.wireOp",EDGE,"E9"),subQ0]}),1.0]])],"derivedFrom":subQ0})])],"isStart":true});}
            var Q62;
            {var subQ0=sQuery(id+"F0.wireOp",EDGE,"E71.trimOffspring");Q62=makeQuery(id+"F1.opExtrude","CAP_EDGE",EDGE,{"disambiguationData":[OSD([subQ0]),TDD([makeQuery(id+"F0.imprint","IMPRINT",EDGE,{"disambiguationData":[TD([[makeQuery(id+"F0.imprint","INTERSECT",VERTEX,{"derivedFrom":[sQuery(id+"F0.wireOp",EDGE,"E6"),subQ0]}),1.0]])],"derivedFrom":subQ0})])],"isStart":false});}
            var Q63;
            {var subQ0=sQuery(id+"F0.wireOp",EDGE,"E71.trimOffspring");Q63=makeQuery(id+"F1.opExtrude","CAP_EDGE",EDGE,{"disambiguationData":[OSD([subQ0]),TDD([makeQuery(id+"F0.imprint","IMPRINT",EDGE,{"disambiguationData":[TD([[makeQuery(id+"F0.imprint","INTERSECT",VERTEX,{"derivedFrom":[sQuery(id+"F0.wireOp",EDGE,"E6"),subQ0]}),1.0]])],"derivedFrom":subQ0})])],"isStart":true});}
            var Q64;
            Q64=makeQuery(id+"F1.opExtrude","CAP_EDGE",EDGE,{"disambiguationData":[OSD([sQuery(id+"F0.wireOp",EDGE,"E7")])],"isStart":false});
            var Q65;
            Q65=makeQuery(id+"F1.opExtrude","CAP_EDGE",EDGE,{"disambiguationData":[OSD([sQuery(id+"F0.wireOp",EDGE,"E8.0"),sQuery(id+"F0.wireOp",EDGE,"E9"),sQuery(id+"F0.wireOp",EDGE,"E10")])],"isStart":false});
            var Q66;
            Q66=makeQuery(id+"F1.opExtrude","CAP_EDGE",EDGE,{"disambiguationData":[OSD([sQuery(id+"F0.wireOp",EDGE,"E6")])],"isStart":false});
            var Q67;
            {var subQ0=sQuery(id+"F0.wireOp",EDGE,"E4.0");Q67=makeQuery(id+"F1.opExtrude","CAP_EDGE",EDGE,{"disambiguationData":[OSD([subQ0]),TDD([makeQuery(id+"F0.imprint","IMPRINT",EDGE,{"disambiguationData":[TD([[makeQuery(id+"F0.imprint","INTERSECT",VERTEX,{"derivedFrom":[subQ0,sQuery(id+"F0.wireOp",EDGE,"E6")]}),1.0]])],"derivedFrom":subQ0})])],"isStart":false});}
            var Q68;
            Q68=makeQuery(id+"F1.opExtrude","CAP_EDGE",EDGE,{"disambiguationData":[OSD([sQuery(id+"F0.wireOp",EDGE,"E5.filletArc")])],"isStart":false});
            var Q69;
            Q69=makeQuery(id+"F1.opExtrude","CAP_EDGE",EDGE,{"disambiguationData":[OSD([sQuery(id+"F0.wireOp",EDGE,"E5.filletArc")])],"isStart":true});
            var Q70;
            {var subQ0=sQuery(id+"F0.wireOp",EDGE,"E0.right");Q70=makeQuery(id+"F1.opExtrude","CAP_EDGE",EDGE,{"disambiguationData":[OSD([subQ0]),TDD([makeQuery(id+"F0.imprint","IMPRINT",EDGE,{"disambiguationData":[TD([[makeQuery(id+"F0.imprint","INTERSECT",VERTEX,{"derivedFrom":[subQ0,sQuery(id+"F0.wireOp",EDGE,"E5.filletArc")]}),1.0]])],"derivedFrom":subQ0})])],"isStart":false});}
            var Q71;
            Q71=makeQuery(id+"F1.opExtrude","CAP_EDGE",EDGE,{"disambiguationData":[OSD([sQuery(id+"F0.wireOp",EDGE,"E33")])],"isStart":false});
            var Q72;
            Q72=makeQuery(id+"F1.opExtrude","CAP_EDGE",EDGE,{"disambiguationData":[OSD([sQuery(id+"F0.wireOp",EDGE,"E33")])],"isStart":true});
            var Q73;
            Q73=makeQuery(id+"F1.opExtrude","CAP_EDGE",EDGE,{"disambiguationData":[OSD([sQuery(id+"F0.wireOp",EDGE,"E26")])],"isStart":false});
            var Q74;
            Q74=makeQuery(id+"F1.opExtrude","CAP_EDGE",EDGE,{"disambiguationData":[OSD([sQuery(id+"F0.wireOp",EDGE,"E26")])],"isStart":true});
            var Q75;
            {var subQ0=sQuery(id+"F0.wireOp",EDGE,"E67.trimOffspring");Q75=makeQuery(id+"F1.opExtrude","CAP_EDGE",EDGE,{"disambiguationData":[OSD([subQ0]),TDD([makeQuery(id+"F0.imprint","IMPRINT",EDGE,{"disambiguationData":[TD([[makeQuery(id+"F0.imprint","INTERSECT",VERTEX,{"derivedFrom":[sQuery(id+"F0.wireOp",EDGE,"E49.0"),subQ0]}),-1.0]])],"derivedFrom":subQ0})])],"isStart":false});}
            var Q76;
            {var subQ0=sQuery(id+"F0.wireOp",EDGE,"E67.trimOffspring");Q76=makeQuery(id+"F1.opExtrude","CAP_EDGE",EDGE,{"disambiguationData":[OSD([subQ0]),TDD([makeQuery(id+"F0.imprint","IMPRINT",EDGE,{"disambiguationData":[TD([[makeQuery(id+"F0.imprint","INTERSECT",VERTEX,{"derivedFrom":[sQuery(id+"F0.wireOp",EDGE,"E49.0"),subQ0]}),-1.0]])],"derivedFrom":subQ0})])],"isStart":true});}
            var Q77;
            Q77=makeQuery(id+"F1.opExtrude","CAP_EDGE",EDGE,{"disambiguationData":[OSD([sQuery(id+"F0.wireOp",EDGE,"E66.trimOffspring")])],"isStart":false});
            var Q78;
            {var subQ0=sQuery(id+"F0.wireOp",EDGE,"E49.0");Q78=makeQuery(id+"F1.opExtrude","CAP_EDGE",EDGE,{"disambiguationData":[OSD([subQ0]),TDD([makeQuery(id+"F0.imprint","IMPRINT",EDGE,{"disambiguationData":[TD([[makeQuery(id+"F0.imprint","INTERSECT",VERTEX,{"derivedFrom":[subQ0,sQuery(id+"F0.wireOp",EDGE,"E67.trimOffspring")]}),1.0]])],"derivedFrom":subQ0})])],"isStart":false});}
            var Q79;
            {var subQ0=sQuery(id+"F0.wireOp",EDGE,"E49.0");Q79=makeQuery(id+"F1.opExtrude","CAP_EDGE",EDGE,{"disambiguationData":[OSD([subQ0]),TDD([makeQuery(id+"F0.imprint","IMPRINT",EDGE,{"disambiguationData":[TD([[makeQuery(id+"F0.imprint","INTERSECT",VERTEX,{"derivedFrom":[subQ0,sQuery(id+"F0.wireOp",EDGE,"E67.trimOffspring")]}),1.0]])],"derivedFrom":subQ0})])],"isStart":true});}
            var Q80;
            {var subQ0=sQuery(id+"F0.wireOp",EDGE,"E67.trimOffspring");Q80=makeQuery(id+"F1.opExtrude","CAP_EDGE",EDGE,{"disambiguationData":[OSD([subQ0]),TDD([makeQuery(id+"F0.imprint","IMPRINT",EDGE,{"disambiguationData":[TD([[makeQuery(id+"F0.imprint","INTERSECT",VERTEX,{"derivedFrom":[sQuery(id+"F0.wireOp",EDGE,"E47.0"),subQ0]}),-1.0]])],"derivedFrom":subQ0})])],"isStart":false});}
            var Q81;
            {var subQ0=sQuery(id+"F0.wireOp",EDGE,"E67.trimOffspring");Q81=makeQuery(id+"F1.opExtrude","CAP_EDGE",EDGE,{"disambiguationData":[OSD([subQ0]),TDD([makeQuery(id+"F0.imprint","IMPRINT",EDGE,{"disambiguationData":[TD([[makeQuery(id+"F0.imprint","INTERSECT",VERTEX,{"derivedFrom":[sQuery(id+"F0.wireOp",EDGE,"E47.0"),subQ0]}),-1.0]])],"derivedFrom":subQ0})])],"isStart":true});}
            var Q82;
            {var subQ0=sQuery(id+"F0.wireOp",EDGE,"E47.0");Q82=makeQuery(id+"F1.opExtrude","CAP_EDGE",EDGE,{"disambiguationData":[OSD([subQ0]),TDD([makeQuery(id+"F0.imprint","IMPRINT",EDGE,{"disambiguationData":[TD([[makeQuery(id+"F0.imprint","INTERSECT",VERTEX,{"derivedFrom":[subQ0,sQuery(id+"F0.wireOp",EDGE,"E67.trimOffspring")]}),1.0]])],"derivedFrom":subQ0})])],"isStart":false});}
            var Q83;
            {var subQ0=sQuery(id+"F0.wireOp",EDGE,"E47.0");Q83=makeQuery(id+"F1.opExtrude","CAP_EDGE",EDGE,{"disambiguationData":[OSD([subQ0]),TDD([makeQuery(id+"F0.imprint","IMPRINT",EDGE,{"disambiguationData":[TD([[makeQuery(id+"F0.imprint","INTERSECT",VERTEX,{"derivedFrom":[subQ0,sQuery(id+"F0.wireOp",EDGE,"E67.trimOffspring")]}),1.0]])],"derivedFrom":subQ0})])],"isStart":true});}
            var Q84;
            {var subQ0=sQuery(id+"F0.wireOp",EDGE,"E45.0");Q84=makeQuery(id+"F1.opExtrude","CAP_EDGE",EDGE,{"disambiguationData":[OSD([subQ0]),TDD([makeQuery(id+"F0.imprint","IMPRINT",EDGE,{"disambiguationData":[TD([[makeQuery(id+"F0.imprint","INTERSECT",VERTEX,{"derivedFrom":[subQ0,sQuery(id+"F0.wireOp",EDGE,"E67.trimOffspring")]}),1.0]])],"derivedFrom":subQ0})])],"isStart":false});}
            var Q85;
            {var subQ0=sQuery(id+"F0.wireOp",EDGE,"E45.0");Q85=makeQuery(id+"F1.opExtrude","CAP_EDGE",EDGE,{"disambiguationData":[OSD([subQ0]),TDD([makeQuery(id+"F0.imprint","IMPRINT",EDGE,{"disambiguationData":[TD([[makeQuery(id+"F0.imprint","INTERSECT",VERTEX,{"derivedFrom":[subQ0,sQuery(id+"F0.wireOp",EDGE,"E67.trimOffspring")]}),1.0]])],"derivedFrom":subQ0})])],"isStart":true});}
            var Q86;
            {var subQ0=sQuery(id+"F0.wireOp",EDGE,"E67.trimOffspring");Q86=makeQuery(id+"F1.opExtrude","CAP_EDGE",EDGE,{"disambiguationData":[OSD([subQ0]),TDD([makeQuery(id+"F0.imprint","IMPRINT",EDGE,{"disambiguationData":[TD([[makeQuery(id+"F0.imprint","INTERSECT",VERTEX,{"derivedFrom":[sQuery(id+"F0.wireOp",EDGE,"E45.0"),subQ0]}),-1.0]])],"derivedFrom":subQ0})])],"isStart":false});}
            var Q87;
            {var subQ0=sQuery(id+"F0.wireOp",EDGE,"E67.trimOffspring");Q87=makeQuery(id+"F1.opExtrude","CAP_EDGE",EDGE,{"disambiguationData":[OSD([subQ0]),TDD([makeQuery(id+"F0.imprint","IMPRINT",EDGE,{"disambiguationData":[TD([[makeQuery(id+"F0.imprint","INTERSECT",VERTEX,{"derivedFrom":[sQuery(id+"F0.wireOp",EDGE,"E45.0"),subQ0]}),-1.0]])],"derivedFrom":subQ0})])],"isStart":true});}
            var Q88;
            Q88=makeQuery(id+"F1.opExtrude","CAP_EDGE",EDGE,{"disambiguationData":[OSD([sQuery(id+"F0.wireOp",EDGE,"E46.0")])],"isStart":false});
            var Q89;
            {var subQ0=sQuery(id+"F0.wireOp",EDGE,"E48.0");Q89=makeQuery(id+"F1.opExtrude","CAP_EDGE",EDGE,{"disambiguationData":[OSD([subQ0]),TDD([makeQuery(id+"F0.imprint","IMPRINT",EDGE,{"disambiguationData":[TD([[makeQuery(id+"F0.imprint","INTERSECT",VERTEX,{"derivedFrom":[subQ0,sQuery(id+"F0.wireOp",EDGE,"E67.trimOffspring")]}),1.0]])],"derivedFrom":subQ0})])],"isStart":false});}
            var Q90;
            {var subQ0=sQuery(id+"F0.wireOp",EDGE,"E27.0");Q90=makeQuery(id+"F1.opExtrude","CAP_EDGE",EDGE,{"disambiguationData":[OSD([subQ0]),TDD([makeQuery(id+"F0.imprint","IMPRINT",EDGE,{"disambiguationData":[TD([[makeQuery(id+"F0.imprint","INTERSECT",VERTEX,{"derivedFrom":[subQ0,sQuery(id+"F0.wireOp",EDGE,"E70.trimOffspring")]}),-1.0]])],"derivedFrom":subQ0})])],"isStart":false});}
            var Q91;
            {var subQ0=sQuery(id+"F0.wireOp",EDGE,"E67.trimOffspring");Q91=makeQuery(id+"F1.opExtrude","CAP_EDGE",EDGE,{"disambiguationData":[OSD([subQ0]),TDD([makeQuery(id+"F0.imprint","IMPRINT",EDGE,{"disambiguationData":[TD([[makeQuery(id+"F0.imprint","INTERSECT",VERTEX,{"derivedFrom":[sQuery(id+"F0.wireOp",EDGE,"E43.0"),subQ0]}),-1.0]])],"derivedFrom":subQ0})])],"isStart":false});}
            var Q92;
            {var subQ0=sQuery(id+"F0.wireOp",EDGE,"E67.trimOffspring");Q92=makeQuery(id+"F1.opExtrude","CAP_EDGE",EDGE,{"disambiguationData":[OSD([subQ0]),TDD([makeQuery(id+"F0.imprint","IMPRINT",EDGE,{"disambiguationData":[TD([[makeQuery(id+"F0.imprint","INTERSECT",VERTEX,{"derivedFrom":[sQuery(id+"F0.wireOp",EDGE,"E43.0"),subQ0]}),-1.0]])],"derivedFrom":subQ0})])],"isStart":true});}
            var Q93;
            Q93=makeQuery(id+"F1.opExtrude","CAP_EDGE",EDGE,{"disambiguationData":[OSD([sQuery(id+"F0.wireOp",EDGE,"E44.0")])],"isStart":false});
            var Q94;
            Q94=makeQuery(id+"F1.opExtrude","CAP_EDGE",EDGE,{"disambiguationData":[OSD([sQuery(id+"F0.wireOp",EDGE,"E43.0")])],"isStart":false});
            var Q95;
            Q95=makeQuery(id+"F1.opExtrude","CAP_EDGE",EDGE,{"disambiguationData":[OSD([sQuery(id+"F0.wireOp",EDGE,"E43.0")])],"isStart":true});
            var Q96;
            {var subQ0=sQuery(id+"F0.wireOp",EDGE,"E42.0");Q96=makeQuery(id+"F1.opExtrude","CAP_EDGE",EDGE,{"disambiguationData":[OSD([subQ0]),TDD([makeQuery(id+"F0.imprint","IMPRINT",EDGE,{"disambiguationData":[TD([[makeQuery(id+"F0.imprint","INTERSECT",VERTEX,{"derivedFrom":[subQ0,sQuery(id+"F0.wireOp",EDGE,"E67.trimOffspring")]}),1.0]])],"derivedFrom":subQ0})])],"isStart":false});}
            var Q97;
            Q97=makeQuery(id+"F1.opExtrude","CAP_EDGE",EDGE,{"disambiguationData":[OSD([sQuery(id+"F0.wireOp",EDGE,"E22.0")])],"isStart":false});
            var Q98;
            Q98=makeQuery(id+"F1.opExtrude","CAP_EDGE",EDGE,{"disambiguationData":[OSD([sQuery(id+"F0.wireOp",EDGE,"E22.0")])],"isStart":true});
            var Q99;
            Q99=makeQuery(id+"F1.opExtrude","CAP_EDGE",EDGE,{"disambiguationData":[OSD([sQuery(id+"F0.wireOp",EDGE,"E21")])],"isStart":false});
            var Q100;
            {var subQ0=sQuery(id+"F0.wireOp",EDGE,"E29.trimOffspring");Q100=makeQuery(id+"F1.opExtrude","CAP_EDGE",EDGE,{"disambiguationData":[OSD([subQ0]),TDD([makeQuery(id+"F0.imprint","IMPRINT",EDGE,{"disambiguationData":[TD([[makeQuery(id+"F0.imprint","INTERSECT",VERTEX,{"derivedFrom":[sQuery(id+"F0.wireOp",EDGE,"E22.0"),subQ0]}),1.0]])],"derivedFrom":subQ0})])],"isStart":false});}
            var Q101;
            {var subQ0=sQuery(id+"F0.wireOp",EDGE,"E29.trimOffspring");Q101=makeQuery(id+"F1.opExtrude","CAP_EDGE",EDGE,{"disambiguationData":[OSD([subQ0]),TDD([makeQuery(id+"F0.imprint","IMPRINT",EDGE,{"disambiguationData":[TD([[makeQuery(id+"F0.imprint","INTERSECT",VERTEX,{"derivedFrom":[sQuery(id+"F0.wireOp",EDGE,"E22.0"),subQ0]}),1.0]])],"derivedFrom":subQ0})])],"isStart":true});}
            var Q102;
            {var subQ0=sQuery(id+"F0.wireOp",EDGE,"E29.trimOffspring");Q102=makeQuery(id+"F1.opExtrude","CAP_EDGE",EDGE,{"disambiguationData":[OSD([subQ0]),TDD([makeQuery(id+"F0.imprint","IMPRINT",EDGE,{"disambiguationData":[TD([[makeQuery(id+"F0.imprint","INTERSECT",VERTEX,{"derivedFrom":[sQuery(id+"F0.wireOp",EDGE,"E25.0"),subQ0]}),-1.0]])],"derivedFrom":subQ0})])],"isStart":false});}
            var Q103;
            {var subQ0=sQuery(id+"F0.wireOp",EDGE,"E29.trimOffspring");Q103=makeQuery(id+"F1.opExtrude","CAP_EDGE",EDGE,{"disambiguationData":[OSD([subQ0]),TDD([makeQuery(id+"F0.imprint","IMPRINT",EDGE,{"disambiguationData":[TD([[makeQuery(id+"F0.imprint","INTERSECT",VERTEX,{"derivedFrom":[sQuery(id+"F0.wireOp",EDGE,"E25.0"),subQ0]}),-1.0]])],"derivedFrom":subQ0})])],"isStart":true});}
            var Q104;
            Q104=makeQuery(id+"F1.opExtrude","CAP_EDGE",EDGE,{"disambiguationData":[OSD([sQuery(id+"F0.wireOp",EDGE,"E59.trimOffspring")])],"isStart":false});
            var Q105;
            Q105=makeQuery(id+"F1.opExtrude","CAP_EDGE",EDGE,{"disambiguationData":[OSD([sQuery(id+"F0.wireOp",EDGE,"E59.trimOffspring")])],"isStart":true});
            var Q106;
            {var subQ0=sQuery(id+"F0.wireOp",EDGE,"E42.0");Q106=makeQuery(id+"F1.opExtrude","CAP_EDGE",EDGE,{"disambiguationData":[OSD([subQ0]),TDD([makeQuery(id+"F0.imprint","IMPRINT",EDGE,{"disambiguationData":[TD([[makeQuery(id+"F0.imprint","INTERSECT",VERTEX,{"derivedFrom":[sQuery(id+"F0.wireOp",EDGE,"E25.0"),subQ0]}),-1.0]])],"derivedFrom":subQ0})])],"isStart":false});}
            var Q107;
            Q107=makeQuery(id+"F1.opExtrude","CAP_EDGE",EDGE,{"disambiguationData":[OSD([sQuery(id+"F0.wireOp",EDGE,"E43.0"),sQuery(id+"F0.wireOp",EDGE,"E84.top")])],"isStart":false});
            var Q108;
            Q108=makeQuery(id+"F1.opExtrude","CAP_EDGE",EDGE,{"disambiguationData":[OSD([sQuery(id+"F0.wireOp",EDGE,"E43.0"),sQuery(id+"F0.wireOp",EDGE,"E84.top")])],"isStart":true});
            var Q109;
            Q109=makeQuery(id+"F1.opExtrude","CAP_EDGE",EDGE,{"disambiguationData":[OSD([sQuery(id+"F0.wireOp",EDGE,"E58.trimOffspring")])],"isStart":false});
            var Q110;
            Q110=makeQuery(id+"F1.opExtrude","CAP_EDGE",EDGE,{"disambiguationData":[OSD([sQuery(id+"F0.wireOp",EDGE,"E56.trimOffspring")])],"isStart":false});
            var Q111;
            Q111=makeQuery(id+"F1.opExtrude","CAP_EDGE",EDGE,{"disambiguationData":[OSD([sQuery(id+"F0.wireOp",EDGE,"E57.trimOffspring")])],"isStart":false});
            var Q112;
            Q112=makeQuery(id+"F1.opExtrude","CAP_EDGE",EDGE,{"disambiguationData":[OSD([sQuery(id+"F0.wireOp",EDGE,"E57.trimOffspring")])],"isStart":true});
            var Q113;
            Q113=makeQuery(id+"F1.opExtrude","CAP_EDGE",EDGE,{"disambiguationData":[OSD([sQuery(id+"F0.wireOp",EDGE,"E44.0"),sQuery(id+"F0.wireOp",EDGE,"E84.bottom")])],"isStart":false});
            var Q114;
            {var subQ0=sQuery(id+"F0.wireOp",EDGE,"E45.0");Q114=makeQuery(id+"F1.opExtrude","CAP_EDGE",EDGE,{"disambiguationData":[OSD([subQ0]),TDD([makeQuery(id+"F0.imprint","IMPRINT",EDGE,{"disambiguationData":[TD([[makeQuery(id+"F0.imprint","INTERSECT",VERTEX,{"derivedFrom":[sQuery(id+"F0.wireOp",EDGE,"E25.0"),subQ0]}),-1.0]])],"derivedFrom":subQ0}),makeQuery(id+"F0.imprint","IMPRINT",EDGE,{"disambiguationData":[TD([[makeQuery(id+"F0.imprint","INTERSECT",VERTEX,{"derivedFrom":[subQ0,sQuery(id+"F0.wireOp",EDGE,"E60.trimOffspring")]}),1.0]])],"derivedFrom":subQ0})])],"isStart":false});}
            var Q115;
            Q115=makeQuery(id+"F1.opExtrude","CAP_EDGE",EDGE,{"disambiguationData":[OSD([sQuery(id+"F0.wireOp",EDGE,"E61.trimOffspring")])],"isStart":false});
            var Q116;
            Q116=makeQuery(id+"F1.opExtrude","CAP_EDGE",EDGE,{"disambiguationData":[OSD([sQuery(id+"F0.wireOp",EDGE,"E60.trimOffspring")])],"isStart":false});
            var Q117;
            Q117=makeQuery(id+"F1.opExtrude","CAP_EDGE",EDGE,{"disambiguationData":[OSD([sQuery(id+"F0.wireOp",EDGE,"E60.trimOffspring")])],"isStart":true});
            var Q118;
            Q118=makeQuery(id+"F1.opExtrude","CAP_EDGE",EDGE,{"disambiguationData":[OSD([sQuery(id+"F0.wireOp",EDGE,"E46.0"),sQuery(id+"F0.wireOp",EDGE,"E85.bottom")])],"isStart":false});
            var Q119;
            {var subQ0=sQuery(id+"F0.wireOp",EDGE,"E47.0");Q119=makeQuery(id+"F1.opExtrude","CAP_EDGE",EDGE,{"disambiguationData":[OSD([subQ0]),TDD([makeQuery(id+"F0.imprint","IMPRINT",EDGE,{"disambiguationData":[TD([[makeQuery(id+"F0.imprint","INTERSECT",VERTEX,{"derivedFrom":[sQuery(id+"F0.wireOp",EDGE,"E25.0"),subQ0]}),-1.0]])],"derivedFrom":subQ0})])],"isStart":false});}
            var Q120;
            {var subQ0=sQuery(id+"F0.wireOp",EDGE,"E47.0");Q120=makeQuery(id+"F1.opExtrude","CAP_EDGE",EDGE,{"disambiguationData":[OSD([subQ0]),TDD([makeQuery(id+"F0.imprint","IMPRINT",EDGE,{"disambiguationData":[TD([[makeQuery(id+"F0.imprint","INTERSECT",VERTEX,{"derivedFrom":[sQuery(id+"F0.wireOp",EDGE,"E25.0"),subQ0]}),-1.0]])],"derivedFrom":subQ0})])],"isStart":true});}
            var Q121;
            Q121=makeQuery(id+"F1.opExtrude","CAP_EDGE",EDGE,{"disambiguationData":[OSD([sQuery(id+"F0.wireOp",EDGE,"E62.trimOffspring")])],"isStart":false});
            var Q122;
            Q122=makeQuery(id+"F1.opExtrude","CAP_EDGE",EDGE,{"disambiguationData":[OSD([sQuery(id+"F0.wireOp",EDGE,"E63.trimOffspring")])],"isStart":false});
            var Q123;
            Q123=makeQuery(id+"F1.opExtrude","CAP_EDGE",EDGE,{"disambiguationData":[OSD([sQuery(id+"F0.wireOp",EDGE,"E63.trimOffspring")])],"isStart":true});
            var Q124;
            {var subQ0=sQuery(id+"F0.wireOp",EDGE,"E48.0");Q124=makeQuery(id+"F1.opExtrude","CAP_EDGE",EDGE,{"disambiguationData":[OSD([subQ0]),TDD([makeQuery(id+"F0.imprint","IMPRINT",EDGE,{"disambiguationData":[TD([[makeQuery(id+"F0.imprint","INTERSECT",VERTEX,{"derivedFrom":[sQuery(id+"F0.wireOp",EDGE,"E25.0"),subQ0]}),-1.0]])],"derivedFrom":subQ0})])],"isStart":false});}
            var Q125;
            {var subQ0=sQuery(id+"F0.wireOp",EDGE,"E49.0");Q125=makeQuery(id+"F1.opExtrude","CAP_EDGE",EDGE,{"disambiguationData":[OSD([subQ0]),TDD([makeQuery(id+"F0.imprint","IMPRINT",EDGE,{"disambiguationData":[TD([[makeQuery(id+"F0.imprint","INTERSECT",VERTEX,{"derivedFrom":[sQuery(id+"F0.wireOp",EDGE,"E25.0"),subQ0]}),-1.0]])],"derivedFrom":subQ0})])],"isStart":false});}
            var Q126;
            {var subQ0=sQuery(id+"F0.wireOp",EDGE,"E49.0");Q126=makeQuery(id+"F1.opExtrude","CAP_EDGE",EDGE,{"disambiguationData":[OSD([subQ0]),TDD([makeQuery(id+"F0.imprint","IMPRINT",EDGE,{"disambiguationData":[TD([[makeQuery(id+"F0.imprint","INTERSECT",VERTEX,{"derivedFrom":[sQuery(id+"F0.wireOp",EDGE,"E25.0"),subQ0]}),-1.0]])],"derivedFrom":subQ0})])],"isStart":true});}
            var Q127;
            Q127=makeQuery(id+"F1.opExtrude","CAP_EDGE",EDGE,{"disambiguationData":[OSD([sQuery(id+"F0.wireOp",EDGE,"E52.0")])],"isStart":false});
            var Q128;
            Q128=makeQuery(id+"F1.opExtrude","CAP_EDGE",EDGE,{"disambiguationData":[OSD([sQuery(id+"F0.wireOp",EDGE,"E52.0")])],"isStart":true});
            var Q129;
            Q129=makeQuery(id+"F1.opExtrude","CAP_EDGE",EDGE,{"disambiguationData":[OSD([sQuery(id+"F0.wireOp",EDGE,"E51.0")])],"isStart":false});
            var Q130;
            {var subQ0=sQuery(id+"F0.wireOp",EDGE,"E27.0");Q130=makeQuery(id+"F1.opExtrude","CAP_EDGE",EDGE,{"disambiguationData":[OSD([subQ0]),TDD([makeQuery(id+"F0.imprint","IMPRINT",EDGE,{"disambiguationData":[TD([[makeQuery(id+"F0.imprint","INTERSECT",VERTEX,{"derivedFrom":[sQuery(id+"F0.wireOp",EDGE,"E25.0"),subQ0]}),1.0]])],"derivedFrom":subQ0})])],"isStart":false});}
            var Q131;
            {var subQ0=sQuery(id+"F0.wireOp",EDGE,"E25.0");Q131=makeQuery(id+"F1.opExtrude","CAP_EDGE",EDGE,{"disambiguationData":[OSD([subQ0]),TDD([makeQuery(id+"F0.imprint","IMPRINT",EDGE,{"disambiguationData":[TD([[makeQuery(id+"F0.imprint","INTERSECT",VERTEX,{"derivedFrom":[subQ0,sQuery(id+"F0.wireOp",EDGE,"E27.0")]}),1.0]])],"derivedFrom":subQ0})])],"isStart":false});}
            var Q132;
            {var subQ0=sQuery(id+"F0.wireOp",EDGE,"E25.0");Q132=makeQuery(id+"F1.opExtrude","CAP_EDGE",EDGE,{"disambiguationData":[OSD([subQ0]),TDD([makeQuery(id+"F0.imprint","IMPRINT",EDGE,{"disambiguationData":[TD([[makeQuery(id+"F0.imprint","INTERSECT",VERTEX,{"derivedFrom":[subQ0,sQuery(id+"F0.wireOp",EDGE,"E47.0")]}),-1.0]])],"derivedFrom":subQ0})])],"isStart":false});}
            var Q133;
            Q133=makeQuery(id+"F1.opExtrude","CAP_EDGE",EDGE,{"disambiguationData":[OSD([sQuery(id+"F0.wireOp",EDGE,"E25.0"),sQuery(id+"F0.wireOp",EDGE,"E85.right")])],"isStart":false});
            var Q134;
            {var subQ0=sQuery(id+"F0.wireOp",EDGE,"E24");Q134=makeQuery(id+"F1.opExtrude","CAP_EDGE",EDGE,{"disambiguationData":[OSD([subQ0]),TDD([makeQuery(id+"F0.imprint","IMPRINT",EDGE,{"disambiguationData":[TD([[makeQuery(id+"F0.imprint","INTERSECT",VERTEX,{"derivedFrom":[subQ0,sQuery(id+"F0.wireOp",EDGE,"E31")]}),-1.0]])],"derivedFrom":subQ0})])],"isStart":false});}
            var Q135;
            {var subQ0=sQuery(id+"F0.wireOp",EDGE,"E24");Q135=makeQuery(id+"F1.opExtrude","CAP_EDGE",EDGE,{"disambiguationData":[OSD([subQ0]),TDD([makeQuery(id+"F0.imprint","IMPRINT",EDGE,{"disambiguationData":[TD([[makeQuery(id+"F0.imprint","INTERSECT",VERTEX,{"derivedFrom":[subQ0,sQuery(id+"F0.wireOp",EDGE,"E31")]}),-1.0]])],"derivedFrom":subQ0})])],"isStart":true});}
            var Q136;
            Q136=makeQuery(id+"F1.opExtrude","CAP_EDGE",EDGE,{"disambiguationData":[OSD([sQuery(id+"F0.wireOp",EDGE,"E84.left")])],"isStart":false});
            var Q137;
            {var subQ0=sQuery(id+"F0.wireOp",EDGE,"E25.0");Q137=makeQuery(id+"F1.opExtrude","CAP_EDGE",EDGE,{"disambiguationData":[OSD([subQ0]),TDD([makeQuery(id+"F0.imprint","IMPRINT",EDGE,{"disambiguationData":[TD([[makeQuery(id+"F0.imprint","INTERSECT",VERTEX,{"derivedFrom":[subQ0,sQuery(id+"F0.wireOp",EDGE,"E29.trimOffspring")]}),-1.0]])],"derivedFrom":subQ0})])],"isStart":false});}
            var Q138;
            {var subQ0=sQuery(id+"F0.wireOp",EDGE,"E48.0");Q138=makeQuery(id+"F1.opExtrude","CAP_EDGE",EDGE,{"disambiguationData":[OSD([subQ0]),TDD([makeQuery(id+"F0.imprint","IMPRINT",EDGE,{"disambiguationData":[TD([[makeQuery(id+"F0.imprint","INTERSECT",VERTEX,{"derivedFrom":[sQuery(id+"F0.wireOp",EDGE,"E25.0"),subQ0]}),-1.0]])],"derivedFrom":subQ0})])],"isStart":true});}
            var Q139;
            {var subQ0=sQuery(id+"F0.wireOp",EDGE,"E27.0");Q139=makeQuery(id+"F1.opExtrude","CAP_EDGE",EDGE,{"disambiguationData":[OSD([subQ0]),TDD([makeQuery(id+"F0.imprint","IMPRINT",EDGE,{"disambiguationData":[TD([[makeQuery(id+"F0.imprint","INTERSECT",VERTEX,{"derivedFrom":[sQuery(id+"F0.wireOp",EDGE,"E25.0"),subQ0]}),1.0]])],"derivedFrom":subQ0})])],"isStart":true});}
            var Q140;
            Q140=makeQuery(id+"F1.opExtrude","CAP_EDGE",EDGE,{"disambiguationData":[OSD([sQuery(id+"F0.wireOp",EDGE,"E46.0"),sQuery(id+"F0.wireOp",EDGE,"E85.bottom")])],"isStart":true});
            var Q141;
            {var subQ0=sQuery(id+"F0.wireOp",EDGE,"E25.0");Q141=makeQuery(id+"F1.opExtrude","CAP_EDGE",EDGE,{"disambiguationData":[OSD([subQ0]),TDD([makeQuery(id+"F0.imprint","IMPRINT",EDGE,{"disambiguationData":[TD([[makeQuery(id+"F0.imprint","INTERSECT",VERTEX,{"derivedFrom":[subQ0,sQuery(id+"F0.wireOp",EDGE,"E47.0")]}),-1.0]])],"derivedFrom":subQ0})])],"isStart":true});}
            var Q142;
            {var subQ0=sQuery(id+"F0.wireOp",EDGE,"E25.0");Q142=makeQuery(id+"F1.opExtrude","CAP_EDGE",EDGE,{"disambiguationData":[OSD([subQ0]),TDD([makeQuery(id+"F0.imprint","IMPRINT",EDGE,{"disambiguationData":[TD([[makeQuery(id+"F0.imprint","INTERSECT",VERTEX,{"derivedFrom":[subQ0,sQuery(id+"F0.wireOp",EDGE,"E27.0")]}),1.0]])],"derivedFrom":subQ0})])],"isStart":true});}
            var Q143;
            {var subQ0=sQuery(id+"F0.wireOp",EDGE,"E3.0");Q143=makeQuery(id+"F1.opExtrude","CAP_EDGE",EDGE,{"disambiguationData":[OSD([subQ0]),TDD([makeQuery(id+"F0.imprint","IMPRINT",EDGE,{"disambiguationData":[TD([[makeQuery(id+"F0.imprint","INTERSECT",VERTEX,{"derivedFrom":[subQ0,sQuery(id+"F0.wireOp",EDGE,"E18")]}),1.0]])],"derivedFrom":subQ0})])],"isStart":true});}
            var Q144;
            Q144=makeQuery(id+"F1.opExtrude","CAP_EDGE",EDGE,{"disambiguationData":[OSD([sQuery(id+"F0.wireOp",EDGE,"E25.0"),sQuery(id+"F0.wireOp",EDGE,"E85.right")])],"isStart":true});
            var Q145;
            Q145=makeQuery(id+"F1.opExtrude","CAP_EDGE",EDGE,{"disambiguationData":[OSD([sQuery(id+"F0.wireOp",EDGE,"E44.0"),sQuery(id+"F0.wireOp",EDGE,"E84.bottom")])],"isStart":true});
            var Q146;
            {var subQ0=sQuery(id+"F0.wireOp",EDGE,"E45.0");Q146=makeQuery(id+"F1.opExtrude","CAP_EDGE",EDGE,{"disambiguationData":[OSD([subQ0]),TDD([makeQuery(id+"F0.imprint","IMPRINT",EDGE,{"disambiguationData":[TD([[makeQuery(id+"F0.imprint","INTERSECT",VERTEX,{"derivedFrom":[sQuery(id+"F0.wireOp",EDGE,"E25.0"),subQ0]}),-1.0]])],"derivedFrom":subQ0}),makeQuery(id+"F0.imprint","IMPRINT",EDGE,{"disambiguationData":[TD([[makeQuery(id+"F0.imprint","INTERSECT",VERTEX,{"derivedFrom":[subQ0,sQuery(id+"F0.wireOp",EDGE,"E60.trimOffspring")]}),1.0]])],"derivedFrom":subQ0})])],"isStart":true});}
            var Q147;
            Q147=makeQuery(id+"F1.opExtrude","CAP_EDGE",EDGE,{"disambiguationData":[OSD([sQuery(id+"F0.wireOp",EDGE,"E89.top")])],"isStart":true});
            var Q148;
            Q148=makeQuery(id+"F1.opExtrude","CAP_EDGE",EDGE,{"disambiguationData":[OSD([sQuery(id+"F0.wireOp",EDGE,"E84.left")])],"isStart":true});
            var Q149;
            {var subQ0=sQuery(id+"F0.wireOp",EDGE,"E25.0");Q149=makeQuery(id+"F1.opExtrude","CAP_EDGE",EDGE,{"disambiguationData":[OSD([subQ0]),TDD([makeQuery(id+"F0.imprint","IMPRINT",EDGE,{"disambiguationData":[TD([[makeQuery(id+"F0.imprint","INTERSECT",VERTEX,{"derivedFrom":[subQ0,sQuery(id+"F0.wireOp",EDGE,"E29.trimOffspring")]}),-1.0]])],"derivedFrom":subQ0})])],"isStart":true});}
            var Q150;
            {var subQ0=sQuery(id+"F0.wireOp",EDGE,"E42.0");Q150=makeQuery(id+"F1.opExtrude","CAP_EDGE",EDGE,{"disambiguationData":[OSD([subQ0]),TDD([makeQuery(id+"F0.imprint","IMPRINT",EDGE,{"disambiguationData":[TD([[makeQuery(id+"F0.imprint","INTERSECT",VERTEX,{"derivedFrom":[sQuery(id+"F0.wireOp",EDGE,"E25.0"),subQ0]}),-1.0]])],"derivedFrom":subQ0})])],"isStart":true});}
            var Q151;
            Q151=makeQuery(id+"F1.opExtrude","CAP_EDGE",EDGE,{"disambiguationData":[OSD([sQuery(id+"F0.wireOp",EDGE,"E19")])],"isStart":true});
            var Q152;
            {var subQ0=sQuery(id+"F0.wireOp",EDGE,"E3.0");Q152=makeQuery(id+"F1.opExtrude","CAP_EDGE",EDGE,{"disambiguationData":[OSD([subQ0]),TDD([makeQuery(id+"F0.imprint","IMPRINT",EDGE,{"disambiguationData":[TD([[makeQuery(id+"F0.imprint","INTERSECT",VERTEX,{"derivedFrom":[sQuery(id+"F0.wireOp",EDGE,"E1.0"),subQ0]}),-1.0]])],"derivedFrom":subQ0})])],"isStart":true});}
            var Q153;
            Q153=makeQuery(id+"F1.opExtrude","CAP_EDGE",EDGE,{"disambiguationData":[OSD([sQuery(id+"F0.wireOp",EDGE,"E58.trimOffspring")])],"isStart":true});
            var Q154;
            {var subQ0=sQuery(id+"F0.wireOp",EDGE,"E42.0");Q154=makeQuery(id+"F1.opExtrude","CAP_EDGE",EDGE,{"disambiguationData":[OSD([subQ0]),TDD([makeQuery(id+"F0.imprint","IMPRINT",EDGE,{"disambiguationData":[TD([[makeQuery(id+"F0.imprint","INTERSECT",VERTEX,{"derivedFrom":[subQ0,sQuery(id+"F0.wireOp",EDGE,"E67.trimOffspring")]}),1.0]])],"derivedFrom":subQ0})])],"isStart":true});}
            var Q155;
            Q155=makeQuery(id+"F1.opExtrude","CAP_EDGE",EDGE,{"disambiguationData":[OSD([sQuery(id+"F0.wireOp",EDGE,"E56.trimOffspring")])],"isStart":true});
            var Q156;
            Q156=makeQuery(id+"F1.opExtrude","CAP_EDGE",EDGE,{"disambiguationData":[OSD([sQuery(id+"F0.wireOp",EDGE,"E44.0")])],"isStart":true});
            var Q157;
            Q157=makeQuery(id+"F1.opExtrude","CAP_EDGE",EDGE,{"disambiguationData":[OSD([sQuery(id+"F0.wireOp",EDGE,"E61.trimOffspring")])],"isStart":true});
            var Q158;
            Q158=makeQuery(id+"F1.opExtrude","CAP_EDGE",EDGE,{"disambiguationData":[OSD([sQuery(id+"F0.wireOp",EDGE,"E46.0")])],"isStart":true});
            var Q159;
            Q159=makeQuery(id+"F1.opExtrude","CAP_EDGE",EDGE,{"disambiguationData":[OSD([sQuery(id+"F0.wireOp",EDGE,"E62.trimOffspring")])],"isStart":true});
            var Q160;
            {var subQ0=sQuery(id+"F0.wireOp",EDGE,"E48.0");Q160=makeQuery(id+"F1.opExtrude","CAP_EDGE",EDGE,{"disambiguationData":[OSD([subQ0]),TDD([makeQuery(id+"F0.imprint","IMPRINT",EDGE,{"disambiguationData":[TD([[makeQuery(id+"F0.imprint","INTERSECT",VERTEX,{"derivedFrom":[subQ0,sQuery(id+"F0.wireOp",EDGE,"E67.trimOffspring")]}),1.0]])],"derivedFrom":subQ0})])],"isStart":true});}
            var Q161;
            Q161=makeQuery(id+"F1.opExtrude","CAP_EDGE",EDGE,{"disambiguationData":[OSD([sQuery(id+"F0.wireOp",EDGE,"E51.0")])],"isStart":true});
            var Q162;
            {var subQ0=sQuery(id+"F0.wireOp",EDGE,"E27.0");Q162=makeQuery(id+"F1.opExtrude","CAP_EDGE",EDGE,{"disambiguationData":[OSD([subQ0]),TDD([makeQuery(id+"F0.imprint","IMPRINT",EDGE,{"disambiguationData":[TD([[makeQuery(id+"F0.imprint","INTERSECT",VERTEX,{"derivedFrom":[subQ0,sQuery(id+"F0.wireOp",EDGE,"E70.trimOffspring")]}),-1.0]])],"derivedFrom":subQ0})])],"isStart":true});}
            var Q163;
            Q163=makeQuery(id+"F1.opExtrude","CAP_EDGE",EDGE,{"disambiguationData":[OSD([sQuery(id+"F0.wireOp",EDGE,"E66.trimOffspring")])],"isStart":true});
            var Q164;
            {var subQ0=sQuery(id+"F0.wireOp",EDGE,"E0.right");Q164=makeQuery(id+"F1.opExtrude","CAP_EDGE",EDGE,{"disambiguationData":[OSD([subQ0]),TDD([makeQuery(id+"F0.imprint","IMPRINT",EDGE,{"disambiguationData":[TD([[makeQuery(id+"F0.imprint","INTERSECT",VERTEX,{"derivedFrom":[subQ0,sQuery(id+"F0.wireOp",EDGE,"E74.bottom"),sQuery(id+"F0.wireOp",EDGE,"E74.right")]}),-1.0]])],"derivedFrom":subQ0})])],"isStart":true});}
            var Q165;
            {var subQ0=sQuery(id+"F0.wireOp",EDGE,"E0.right");Q165=makeQuery(id+"F1.opExtrude","CAP_EDGE",EDGE,{"disambiguationData":[OSD([subQ0]),TDD([makeQuery(id+"F0.imprint","IMPRINT",EDGE,{"disambiguationData":[TD([[makeQuery(id+"F0.imprint","INTERSECT",VERTEX,{"derivedFrom":[subQ0,sQuery(id+"F0.wireOp",EDGE,"E78.bottom"),sQuery(id+"F0.wireOp",EDGE,"E78.left")]}),-1.0]])],"derivedFrom":subQ0})])],"isStart":true});}
            var Q166;
            {var subQ0=sQuery(id+"F0.wireOp",EDGE,"E0.right");Q166=makeQuery(id+"F1.opExtrude","CAP_EDGE",EDGE,{"disambiguationData":[OSD([subQ0]),TDD([makeQuery(id+"F0.imprint","IMPRINT",EDGE,{"disambiguationData":[TD([[makeQuery(id+"F0.imprint","INTERSECT",VERTEX,{"derivedFrom":[subQ0,sQuery(id+"F0.wireOp",EDGE,"E78.bottom"),sQuery(id+"F0.wireOp",EDGE,"E78.left")]}),-1.0]])],"derivedFrom":subQ0})])],"isStart":false});}
            var Q167;
            Q167=makeQuery(id+"F1.opExtrude","CAP_EDGE",EDGE,{"disambiguationData":[OSD([sQuery(id+"F0.wireOp",EDGE,"E0.right"),sQuery(id+"F0.wireOp",EDGE,"E68.right")])],"isStart":true});
            var Q168;
            Q168=makeQuery(id+"F1.opExtrude","CAP_EDGE",EDGE,{"disambiguationData":[OSD([sQuery(id+"F0.wireOp",EDGE,"E8.0"),sQuery(id+"F0.wireOp",EDGE,"E9"),sQuery(id+"F0.wireOp",EDGE,"E10")])],"isStart":true});
            var Q169;
            Q169=makeQuery(id+"F1.opExtrude","CAP_EDGE",EDGE,{"disambiguationData":[OSD([sQuery(id+"F0.wireOp",EDGE,"E7")])],"isStart":true});
            var Q170;
            {var subQ0=sQuery(id+"F0.wireOp",EDGE,"E4.0");Q170=makeQuery(id+"F1.opExtrude","CAP_EDGE",EDGE,{"disambiguationData":[OSD([subQ0]),TDD([makeQuery(id+"F0.imprint","IMPRINT",EDGE,{"disambiguationData":[TD([[makeQuery(id+"F0.imprint","INTERSECT",VERTEX,{"derivedFrom":[subQ0,sQuery(id+"F0.wireOp",EDGE,"E10")]}),1.0]])],"derivedFrom":subQ0})])],"isStart":true});}
            var Q171;
            {var subQ0=sQuery(id+"F0.wireOp",EDGE,"E4.0");Q171=makeQuery(id+"F1.opExtrude","CAP_EDGE",EDGE,{"disambiguationData":[OSD([subQ0]),TDD([makeQuery(id+"F0.imprint","IMPRINT",EDGE,{"disambiguationData":[TD([[makeQuery(id+"F0.imprint","INTERSECT",VERTEX,{"derivedFrom":[subQ0,sQuery(id+"F0.wireOp",EDGE,"E6")]}),1.0]])],"derivedFrom":subQ0})])],"isStart":true});}
            var Q172;
            Q172=makeQuery(id+"F1.opExtrude","CAP_EDGE",EDGE,{"disambiguationData":[OSD([sQuery(id+"F0.wireOp",EDGE,"E6")])],"isStart":true});
            var Q173;
            {var subQ0=sQuery(id+"F0.wireOp",EDGE,"E0.right");Q173=makeQuery(id+"F1.opExtrude","CAP_EDGE",EDGE,{"disambiguationData":[OSD([subQ0]),TDD([makeQuery(id+"F0.imprint","IMPRINT",EDGE,{"disambiguationData":[TD([[makeQuery(id+"F0.imprint","INTERSECT",VERTEX,{"derivedFrom":[subQ0,sQuery(id+"F0.wireOp",EDGE,"E5.filletArc")]}),1.0]])],"derivedFrom":subQ0})])],"isStart":true});}
            var Q174;
            Q174=makeQuery(id+"F1.opExtrude","CAP_EDGE",EDGE,{"disambiguationData":[OSD([sQuery(id+"F0.wireOp",EDGE,"E16.0"),sQuery(id+"F0.wireOp",EDGE,"E17"),sQuery(id+"F0.wireOp",EDGE,"E18")])],"isStart":true});
            var Q175;
            {var subQ0=sQuery(id+"F0.wireOp",EDGE,"E4.0");Q175=makeQuery(id+"F1.opExtrude","CAP_EDGE",EDGE,{"disambiguationData":[OSD([subQ0]),TDD([makeQuery(id+"F0.imprint","IMPRINT",EDGE,{"disambiguationData":[TD([[makeQuery(id+"F0.imprint","INTERSECT",VERTEX,{"derivedFrom":[subQ0,sQuery(id+"F0.wireOp",EDGE,"E14")]}),-1.0]])],"derivedFrom":subQ0})])],"isStart":true});}
            var Q176;
            Q176=makeQuery(id+"F1.opExtrude","CAP_EDGE",EDGE,{"disambiguationData":[OSD([sQuery(id+"F0.wireOp",EDGE,"E14")])],"isStart":true});
            var Q177;
            {var subQ0=sQuery(id+"F0.wireOp",EDGE,"E3.0");Q177=makeQuery(id+"F1.opExtrude","CAP_EDGE",EDGE,{"disambiguationData":[OSD([subQ0]),TDD([makeQuery(id+"F0.imprint","IMPRINT",EDGE,{"disambiguationData":[TD([[makeQuery(id+"F0.imprint","INTERSECT",VERTEX,{"derivedFrom":[subQ0,sQuery(id+"F0.wireOp",EDGE,"E14")]}),1.0]])],"derivedFrom":subQ0})])],"isStart":true});}
            var Q178;
            Q178=makeQuery(id+"F1.opExtrude","CAP_EDGE",EDGE,{"disambiguationData":[OSD([sQuery(id+"F0.wireOp",EDGE,"E0.right"),sQuery(id+"F0.wireOp",EDGE,"E64.right")])],"isStart":true});
            var Q179;
            {var subQ0=sQuery(id+"F0.wireOp",EDGE,"E0.right");Q179=makeQuery(id+"F1.opExtrude","CAP_EDGE",EDGE,{"disambiguationData":[OSD([subQ0]),TDD([makeQuery(id+"F0.imprint","IMPRINT",EDGE,{"disambiguationData":[TD([[makeQuery(id+"F0.imprint","INTERSECT",VERTEX,{"derivedFrom":[subQ0,sQuery(id+"F0.wireOp",EDGE,"E72.top"),sQuery(id+"F0.wireOp",EDGE,"E72.left")]}),1.0]])],"derivedFrom":subQ0})])],"isStart":true});}
            var Q180;
            {var subQ0=sQuery(id+"F0.wireOp",EDGE,"E0.right");Q180=makeQuery(id+"F1.opExtrude","CAP_EDGE",EDGE,{"disambiguationData":[OSD([subQ0]),TDD([makeQuery(id+"F0.imprint","IMPRINT",EDGE,{"disambiguationData":[TD([[makeQuery(id+"F0.imprint","INTERSECT",VERTEX,{"derivedFrom":[subQ0,sQuery(id+"F0.wireOp",EDGE,"E34")]}),-1.0]])],"derivedFrom":subQ0})])],"isStart":true});}
            fillet(context, id + "F2", {"entities" : qUnion([Q0, Q1, Q2, Q3, Q4, Q5, Q6, Q7, Q8, Q9, Q10, Q11, Q12, Q13, Q14, Q15, Q16, Q17, Q18, Q19, Q20, Q21, Q22, Q23, Q24, Q25, Q26, Q27, Q28, Q29, Q30, Q31, Q32, Q33, Q34, Q35, Q36, Q37, Q38, Q39, Q40, Q41, Q42, Q43, Q44, Q45, Q46, Q47, Q48, Q49, Q50, Q51, Q52, Q53, Q54, Q55, Q56, Q57, Q58, Q59, Q60, Q61, Q62, Q63, Q64, Q65, Q66, Q67, Q68, Q69, Q70, Q71, Q72, Q73, Q74, Q75, Q76, Q77, Q78, Q79, Q80, Q81, Q82, Q83, Q84, Q85, Q86, Q87, Q88, Q89, Q90, Q91, Q92, Q93, Q94, Q95, Q96, Q97, Q98, Q99, Q100, Q101, Q102, Q103, Q104, Q105, Q106, Q107, Q108, Q109, Q110, Q111, Q112, Q113, Q114, Q115, Q116, Q117, Q118, Q119, Q120, Q121, Q122, Q123, Q124, Q125, Q126, Q127, Q128, Q129, Q130, Q131, Q132, Q133, Q134, Q135, Q136, Q137, Q138, Q139, Q140, Q141, Q142, Q143, Q144, Q145, Q146, Q147, Q148, Q149, Q150, Q151, Q152, Q153, Q154, Q155, Q156, Q157, Q158, Q159, Q160, Q161, Q162, Q163, Q164, Q165, Q166, Q167, Q168, Q169, Q170, Q171, Q172, Q173, Q174, Q175, Q176, Q177, Q178, Q179, Q180]), "radius" : .2 * mm, "tangentPropagation" : true, "allowEdgeOverflow" : false});
        }
        {
            var Q0;
            Q0=qCreatedBy(makeId("Front.planeOp"),FACE);
            var sketch = newSketch(context, id + "F3", { "sketchPlane" : qUnion([Q0])});
            skLineSegment(sketch, "E90", {"start": v(-39.91, 42.55) * mm, "end": v(-47.26, 35.08) * mm});
            skLineSegment(sketch, "E91", {"start": v(-47.26, 35.08) * mm, "end": v(-47.26, 41.21) * mm});
            skLineSegment(sketch, "E92", {"start": v(-47.26, 41.21) * mm, "end": v(-46.87, 41.74) * mm});
            skLineSegment(sketch, "E93", {"start": v(-46.87, 41.74) * mm, "end": v(-46.33, 42.27) * mm});
            skLineSegment(sketch, "E94", {"start": v(-46.33, 42.27) * mm, "end": v(-45.65, 42.55) * mm});
            skLineSegment(sketch, "E95", {"start": v(-45.65, 42.55) * mm, "end": v(-39.91, 42.55) * mm});
            skLineSegment(sketch, "E96", {"start": v(-7.8, 42.55) * mm, "end": v(-2.2, 42.55) * mm});
            skLineSegment(sketch, "E97", {"start": v(-2.2, 42.55) * mm, "end": v(-1.5, 42.4) * mm});
            skLineSegment(sketch, "E98", {"start": v(-1.5, 42.4) * mm, "end": v(-0.9, 41.94) * mm});
            skLineSegment(sketch, "E99", {"start": v(-0.9, 41.94) * mm, "end": v(-0.41, 41.2) * mm});
            skLineSegment(sketch, "E100", {"start": v(-0.41, 41.2) * mm, "end": v(-0.28, 40.5) * mm});
            skLineSegment(sketch, "E101", {"start": v(-0.28, 40.5) * mm, "end": v(-0.28, 35.04) * mm});
            skLineSegment(sketch, "E102", {"start": v(-0.28, 35.04) * mm, "end": v(-7.8, 42.55) * mm});
            skSolve(sketch);
        }
        {
            var Q0;
            Q0 = qSketchRegion(id + "F3", true);
            extrude(context, id + "F4", {"entities" : qUnion([Q0]), "operationType" : NewBodyOperationType.ADD, "depth" : .3 * mm, "symmetric" : true});
        }
    });
